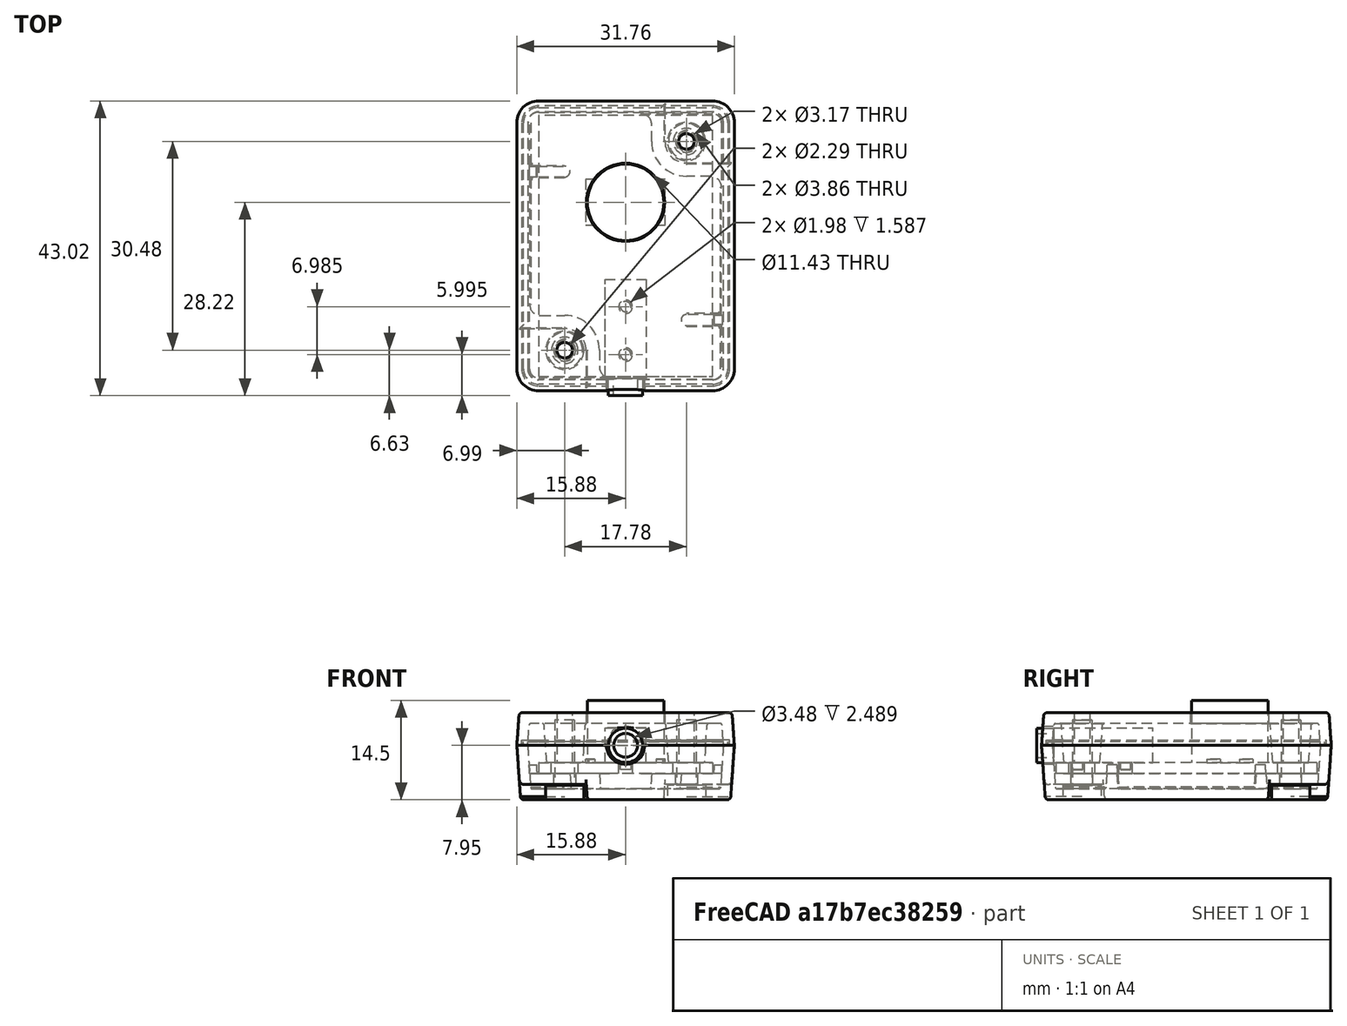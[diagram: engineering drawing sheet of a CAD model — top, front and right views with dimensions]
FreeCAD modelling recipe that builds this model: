
FCSTD DOCUMENT  (FreeCAD 0.20R29603 (Git))
Label: pump-fob-case-v2
License: All rights reserved
LicenseURL: http://en.wikipedia.org/wiki/All_rights_reserved
objects: Sketcher::SketchObject×21, PartDesign::Body×13, PartDesign::Pad×11, PartDesign::Pocket×10, PartDesign::FeatureBase×8, App::DocumentObjectGroup×5, PartDesign::Fillet×5, Mesh::Feature×2, Part::MultiFuse×1, Part::Feature×1
note: 96 computed .brp shape members not serialized (recipe doc carries the construction recipe); baked Part::Feature solids carry a one-line shape summary decoded from their .brp

FEATURE [Sketcher::SketchObject] Sketch  label="audio jack plan"
  FullyConstrained = true
  MapMode = 5
  Support = -> [XY_Plane]
  sketch-geometry (6):
    g0: LineSegment StartX=-2.9972 StartY=14.478 StartZ=0 EndX=2.9972 EndY=14.478 EndZ=0
    g1: LineSegment StartX=2.9972 StartY=14.478 StartZ=0 EndX=2.9972 EndY=0 EndZ=0
    g2: LineSegment StartX=2.9972 StartY=0 StartZ=0 EndX=-2.9972 EndY=0 EndZ=0
    g3: LineSegment StartX=-2.9972 StartY=0 StartZ=0 EndX=-2.9972 EndY=14.478 EndZ=0
    g4: LineSegment StartX=-2.9972 StartY=14.478 StartZ=0 EndX=0 EndY=7.239 EndZ=0
    g5: LineSegment StartX=0 StartY=7.239 StartZ=0 EndX=2.9972 EndY=0 EndZ=0
  constraints (17):
    c: Coincident(g0,g1)
    c: Coincident(g1,g2)
    c: Coincident(g2,g3)
    c: Coincident(g3,g0)
    c: Horizontal(g0)
    c: Horizontal(g2)
    c: Vertical(g1)
    c: Vertical(g3)
    c: PointOnObject(g-1,g2)
    c: Coincident(g0,g4)
    c: Coincident(g4,g5)
    c: Coincident(g5,g1)
    c: Parallel(g4,g5)
    c: Equal(g4,g5)
    c: PointOnObject(g4,g-2)
    c: DistanceY(g1,g1) = 14.478
    c: DistanceX(g2,g2) = 5.9944
FEATURE [PartDesign::Pad] Pad  label="audio jack slab"
  Direction = (0,0,1)
  Length = 5.08
  Length2 = 10
  Profile = -> Sketch
  ReferenceAxis = -> Sketch [N_Axis]
  Type = 0
FEATURE [Sketcher::SketchObject] Sketch001  label="audio jack port plan"
  ExternalGeometry = -> [Pad]
  FullyConstrained = true
  MapMode = 5
  Placement = pos=(0,0,0) rot=(1,0,0;1.5708rad)
  Support = -> [Pad]
  sketch-geometry (4):
    g0: LineSegment StartX=-2.9972 StartY=5.08 StartZ=0 EndX=0 EndY=2.54 EndZ=0
    g1: LineSegment StartX=0 StartY=2.54 StartZ=0 EndX=2.9972 EndY=0 EndZ=0
    g2: Circle CenterX=0 CenterY=2.54 CenterZ=0 NormalX=0 NormalY=0 NormalZ=1 AngleXU=0 Radius=2.5019
    g3: Circle CenterX=0 CenterY=2.54 CenterZ=0 NormalX=0 NormalY=0 NormalZ=1 AngleXU=0 Radius=1.7399
  constraints (9):
    c: Coincident(g0,g-3)
    c: Coincident(g0,g1)
    c: Coincident(g1,g-4)
    c: Parallel(g1,g0)
    c: Equal(g0,g1)
    c: Coincident(g2,g0)
    c: Coincident(g3,g2)
    c: Diameter(g2) = 5.0038
    c: Diameter(g3) = 3.4798
FEATURE [PartDesign::Pad] Pad001  label="audio jack with port"
  BaseFeature = -> Pad
  Direction = (0,-1,2e-16)
  Length = 2.4892
  Length2 = 10
  Profile = -> Sketch001
  ReferenceAxis = -> Sketch001 [N_Axis]
  Type = 0
FEATURE [Sketcher::SketchObject] Sketch002  label="audio jack post plan"
  FullyConstrained = true
  MapMode = 5
  Placement = pos=(0,0,0) rot=(1,0,0;3.14159rad)
  Support = -> [Pad001]
  sketch-geometry (2):
    g0: Circle CenterX=0 CenterY=-3.5052 CenterZ=0 NormalX=0 NormalY=0 NormalZ=1 AngleXU=0 Radius=0.7493
    g1: Circle CenterX=0 CenterY=-10.5156 CenterZ=0 NormalX=0 NormalY=0 NormalZ=1 AngleXU=0 Radius=0.7493
  constraints (6):
    c: PointOnObject(g0,g-2)
    c: PointOnObject(g1,g-2)
    c: Equal(g1,g0)
    c: Diameter(g1) = 1.4986
    c: DistanceY(g0,g-1) = 3.5052
    c: DistanceY(g1,g0) = 7.0104
FEATURE [PartDesign::Pad] Pad002  label="audio jack with posts"
  BaseFeature = -> Pad001
  Direction = (0,0,-1)
  Length = 1.016
  Length2 = 10
  Profile = -> Sketch002
  ReferenceAxis = -> Sketch002 [N_Axis]
  Type = 0
FEATURE [PartDesign::Body] Body  label="audio jack body"
  Group = -> [Sketch,Pad,Sketch001,Pad001,Sketch002,Pad002]
  Origin = -> Origin
  Tip = -> Pad002
FEATURE [Sketcher::SketchObject] Sketch003  label="switch button plan"
  FullyConstrained = true
  MapMode = 5
  Support = -> [XY_Plane001]
  sketch-geometry (1):
    g0: Circle CenterX=0 CenterY=0 CenterZ=0 NormalX=0 NormalY=0 NormalZ=1 AngleXU=0 Radius=5.588
  constraints (2):
    c: Coincident(g0,g-1)
    c: Diameter(g0) = 11.176
FEATURE [PartDesign::Pad] Pad003  label="switch button block"
  Direction = (0,0,1)
  Length = 9.0932
  Length2 = 10
  Profile = -> Sketch003
  ReferenceAxis = -> Sketch003 [N_Axis]
  Type = 0
FEATURE [Sketcher::SketchObject] Sketch004  label="switch lead plan"
  FullyConstrained = true
  MapMode = 5
  Placement = pos=(0,0,0) rot=(1,0,0;3.14159rad)
  Support = -> [Pad003]
  sketch-geometry (22):
    g0: LineSegment StartX=-3.3401 StartY=5.8039 StartZ=0 EndX=-1.397 EndY=5.8039 EndZ=0
    g1: LineSegment StartX=-1.397 StartY=5.8039 StartZ=0 EndX=-1.397 EndY=2.54 EndZ=0
    g2: LineSegment StartX=-1.397 StartY=2.54 StartZ=0 EndX=-3.3401 EndY=2.54 EndZ=0
    g3: LineSegment StartX=-3.3401 StartY=2.54 StartZ=0 EndX=-3.3401 EndY=5.8039 EndZ=0
    g4: LineSegment StartX=1.397 StartY=5.8039 StartZ=0 EndX=3.3401 EndY=5.8039 EndZ=0
    g5: LineSegment StartX=3.3401 StartY=5.8039 StartZ=0 EndX=3.3401 EndY=2.54 EndZ=0
    g6: LineSegment StartX=3.3401 StartY=2.54 StartZ=0 EndX=1.397 EndY=2.54 EndZ=0
    g7: LineSegment StartX=1.397 StartY=2.54 StartZ=0 EndX=1.397 EndY=5.8039 EndZ=0
    g8: LineSegment StartX=1.397 StartY=-2.54 StartZ=0 EndX=3.3401 EndY=-2.54 EndZ=0
    g9: LineSegment StartX=3.3401 StartY=-2.54 StartZ=0 EndX=3.3401 EndY=-5.8039 EndZ=0
    g10: LineSegment StartX=3.3401 StartY=-5.8039 StartZ=0 EndX=1.397 EndY=-5.8039 EndZ=0
    g11: LineSegment StartX=1.397 StartY=-5.8039 StartZ=0 EndX=1.397 EndY=-2.54 EndZ=0
    g12: LineSegment StartX=-3.3401 StartY=-2.54 StartZ=0 EndX=-1.397 EndY=-2.54 EndZ=0
    g13: LineSegment StartX=-1.397 StartY=-2.54 StartZ=0 EndX=-1.397 EndY=-5.8039 EndZ=0
    g14: LineSegment StartX=-1.397 StartY=-5.8039 StartZ=0 EndX=-3.3401 EndY=-5.8039 EndZ=0
    g15: LineSegment StartX=-3.3401 StartY=-5.8039 StartZ=0 EndX=-3.3401 EndY=-2.54 EndZ=0
    g16: LineSegment StartX=-1.397 StartY=2.54 StartZ=0 EndX=1.397 EndY=2.54 EndZ=0
    g17: LineSegment StartX=1.397 StartY=2.54 StartZ=0 EndX=1.397 EndY=-2.54 EndZ=0
    g18: LineSegment StartX=1.397 StartY=-2.54 StartZ=0 EndX=-1.397 EndY=-2.54 EndZ=0
    g19: LineSegment StartX=-1.397 StartY=-2.54 StartZ=0 EndX=-1.397 EndY=2.54 EndZ=0
    g20: LineSegment StartX=-1.397 StartY=2.54 StartZ=0 EndX=0 EndY=0 EndZ=0
    g21: LineSegment StartX=0 StartY=0 StartZ=0 EndX=1.397 EndY=-2.54 EndZ=0
  constraints (60):
    c: Coincident(g0,g1)
    c: Coincident(g1,g2)
    c: Coincident(g2,g3)
    c: Coincident(g3,g0)
    c: Horizontal(g0)
    c: Horizontal(g2)
    c: Vertical(g1)
    c: Vertical(g3)
    c: Coincident(g4,g5)
    c: Coincident(g5,g6)
    c: Coincident(g6,g7)
    c: Coincident(g7,g4)
    c: Horizontal(g4)
    c: Horizontal(g6)
    c: Vertical(g5)
    c: Vertical(g7)
    c: Coincident(g8,g9)
    c: Coincident(g9,g10)
    c: Coincident(g10,g11)
    c: Coincident(g11,g8)
    c: Horizontal(g8)
    c: Horizontal(g10)
    c: Vertical(g9)
    c: Vertical(g11)
    c: Coincident(g12,g13)
    c: Coincident(g13,g14)
    c: Coincident(g14,g15)
    c: Coincident(g15,g12)
    c: Horizontal(g12)
    c: Horizontal(g14)
    c: Vertical(g13)
    c: Vertical(g15)
    c: Coincident(g16,g17)
    c: Coincident(g17,g18)
    c: Coincident(g18,g19)
    c: Coincident(g19,g16)
    c: Horizontal(g16)
    c: Horizontal(g18)
    c: Vertical(g17)
    c: Vertical(g19)
    c: Coincident(g16,g1)
    c: Coincident(g17,g8)
    c: Coincident(g6,g16)
    c: Coincident(g12,g18)
    c: Coincident(g1,g20)
    c: Coincident(g20,g-1)
    c: Coincident(g20,g21)
    c: Coincident(g21,g8)
    c: Parallel(g21,g20)
    c: Equal(g20,g21)
    c: Equal(g6,g8)
    c: Equal(g8,g12)
    c: Equal(g12,g2)
    c: Equal(g7,g1)
    c: Equal(g1,g13)
    c: Equal(g13,g11)
    c: DistanceX(g13,g10) = 2.794
    c: DistanceY(g14,g0) = 11.6078
    c: DistanceX(g0,g4) = 6.6802
    c: DistanceY(g8,g5) = 5.08
FEATURE [PartDesign::Pad] Pad004  label="switch with leads"
  BaseFeature = -> Pad003
  Direction = (0,0,-1)
  Length = 0.508
  Length2 = 10
  Profile = -> Sketch004
  ReferenceAxis = -> Sketch004 [N_Axis]
  Reversed = true
  Type = 0
FEATURE [PartDesign::Body] Body001  label="switch body"
  Group = -> [Sketch003,Pad003,Sketch004,Pad004]
  Origin = -> Origin001
  Tip = -> Pad004
FEATURE [PartDesign::FeatureBase] Clone
  BaseFeature = -> Body
FEATURE [PartDesign::Body] Body002  label="audio jack clone"
  Group = -> [Clone]
  Origin = -> Origin002
  Placement = pos=(0,-0.3302,0) rot=(0,0,1;0rad)
  Tip = -> Clone
FEATURE [PartDesign::FeatureBase] Clone001
  BaseFeature = -> Body001
FEATURE [PartDesign::Body] Body003  label="switch clone"
  Group = -> [Clone001]
  Origin = -> Origin003
  Placement = pos=(0,25.4,0) rot=(0,0,1;1.5708rad)
  Tip = -> Clone001
FEATURE [Sketcher::SketchObject] Sketch005  label="bare pcb plan"
  FullyConstrained = true
  MapMode = 5
  Support = -> [XY_Plane004]
  sketch-geometry (14):
    g0: LineSegment StartX=-12.7 StartY=0 StartZ=0 EndX=12.7 EndY=0 EndZ=0
    g1: LineSegment StartX=12.7 StartY=0 StartZ=0 EndX=12.7 EndY=38.1 EndZ=0
    g2: LineSegment StartX=12.7 StartY=38.1 StartZ=0 EndX=-12.7 EndY=38.1 EndZ=0
    g3: LineSegment StartX=-12.7 StartY=38.1 StartZ=0 EndX=-12.7 EndY=0 EndZ=0
    g4: LineSegment StartX=12.7 StartY=38.1 StartZ=0 EndX=8.89 EndY=38.1 EndZ=0
    g5: LineSegment StartX=8.89 StartY=38.1 StartZ=0 EndX=8.89 EndY=34.29 EndZ=0
    g6: LineSegment StartX=-12.7 StartY=0 StartZ=0 EndX=-8.89 EndY=0 EndZ=0
    g7: LineSegment StartX=-8.89 StartY=0 StartZ=0 EndX=-8.89 EndY=3.81 EndZ=0
    g8: Circle CenterX=-8.89 CenterY=3.81 CenterZ=0 NormalX=0 NormalY=0 NormalZ=1 AngleXU=0 Radius=1.9304
    g9: Circle CenterX=8.89 CenterY=34.29 CenterZ=0 NormalX=0 NormalY=0 NormalZ=1 AngleXU=0 Radius=1.9304
    g10: LineSegment StartX=-12.7 StartY=38.1 StartZ=0 EndX=0 EndY=19.05 EndZ=0
    g11: LineSegment StartX=0 StartY=19.05 StartZ=0 EndX=12.7 EndY=0 EndZ=0
    g12: Circle CenterX=0 CenterY=3.175 CenterZ=0 NormalX=0 NormalY=0 NormalZ=1 AngleXU=0 Radius=0.9906
    g13: Circle CenterX=0 CenterY=10.16 CenterZ=0 NormalX=0 NormalY=0 NormalZ=1 AngleXU=0 Radius=0.9906
  constraints (39):
    c: Coincident(g0,g1)
    c: Coincident(g1,g2)
    c: Coincident(g2,g3)
    c: Coincident(g3,g0)
    c: Horizontal(g0)
    c: Horizontal(g2)
    c: Vertical(g1)
    c: Vertical(g3)
    c: DistanceY(g1,g1) = 38.1
    c: DistanceX(g2,g2) = 25.4
    c: Coincident(g1,g4)
    c: Coincident(g4,g5)
    c: Vertical(g5)
    c: Coincident(g0,g6)
    c: Coincident(g6,g7)
    c: Vertical(g7)
    c: Equal(g5,g7)
    c: Equal(g4,g6)
    c: Horizontal(g6)
    c: Horizontal(g4)
    c: DistanceX(g0,g6) = 3.81
    c: DistanceY(g0,g7) = 3.81
    c: Coincident(g8,g7)
    c: Coincident(g9,g5)
    c: Equal(g9,g8)
    c: Diameter(g9) = 3.8608
    c: PointOnObject(g-1,g0)
    c: Coincident(g2,g10)
    c: PointOnObject(g10,g-2)
    c: Coincident(g10,g11)
    c: Coincident(g11,g0)
    c: Parallel(g11,g10)
    c: Equal(g10,g11)
    c: PointOnObject(g12,g-2)
    c: PointOnObject(g13,g-2)
    c: Equal(g12,g13)
    c: Diameter(g12) = 1.9812
    c: DistanceY(g0,g12) = 3.175
    c: DistanceY(g12,g13) = 6.985
FEATURE [PartDesign::Pad] Pad005  label="bare pcb slab"
  Direction = (0,0,1)
  Length = 1.5875
  Length2 = 10
  Profile = -> Sketch005
  ReferenceAxis = -> Sketch005 [N_Axis]
  Reversed = true
  Type = 0
FEATURE [PartDesign::Body] Body004  label="bare pcb body"
  Group = -> [Sketch005,Pad005]
  Origin = -> Origin004
  Tip = -> Pad005
FEATURE [PartDesign::FeatureBase] Clone002
  BaseFeature = -> Body004
FEATURE [PartDesign::Body] Body005  label="bare pcb clone"
  Group = -> [Clone002]
  Origin = -> Origin005
  Tip = -> Clone002
FEATURE [Part::MultiFuse] Fusion  label="populated pcb"
  Shapes = -> [Body002,Body003,Body005]
FEATURE [App::DocumentObjectGroup] Group  label="pcb parts"
  Group = -> [Body,Body001,Body004,Fusion]
FEATURE [PartDesign::FeatureBase] Clone003
  BaseFeature = -> Fusion
FEATURE [PartDesign::Body] Body006  label="populated pcb clone"
  Group = -> [Clone003]
  Origin = -> Origin006
  Placement = pos=(0,0,-2.54) rot=(0,0,1;0rad)
  Tip = -> Clone003
FEATURE [Sketcher::SketchObject] Sketch006  label="bottom shell outline"
  FullyConstrained = true
  MapMode = 5
  Support = -> [XY_Plane007]
  sketch-geometry (37):
    g0: LineSegment StartX=0 StartY=1.0795 StartZ=0 EndX=12.7 EndY=1.0795 EndZ=0
    g1: LineSegment StartX=12.7 StartY=1.0795 StartZ=0 EndX=14.2875 EndY=1.0795 EndZ=0
    g2: LineSegment StartX=14.2875 StartY=1.0795 StartZ=0 EndX=15.875 EndY=1.0795 EndZ=0
    g3: LineSegment StartX=12.7 StartY=1.0795 StartZ=0 EndX=12.7 EndY=37.0205 EndZ=0
    g4: LineSegment StartX=12.7 StartY=37.0205 StartZ=0 EndX=14.2875 EndY=37.0205 EndZ=0
    g5: LineSegment StartX=14.2875 StartY=37.0205 StartZ=0 EndX=15.875 EndY=37.0205 EndZ=0
    g6: LineSegment StartX=12.7 StartY=40.1955 StartZ=0 EndX=12.7 EndY=38.608 EndZ=0
    g7: LineSegment StartX=12.7 StartY=38.608 StartZ=0 EndX=12.7 EndY=37.0205 EndZ=0
    g8: LineSegment StartX=12.7 StartY=37.0205 StartZ=0 EndX=-12.7 EndY=37.0205 EndZ=0
    g9: LineSegment StartX=-12.7 StartY=37.0205 StartZ=0 EndX=-12.7 EndY=38.608 EndZ=0
    g10: LineSegment StartX=-12.7 StartY=38.608 StartZ=0 EndX=-12.7 EndY=40.1955 EndZ=0
    g11: LineSegment StartX=-15.875 StartY=37.0205 StartZ=0 EndX=-14.2875 EndY=37.0205 EndZ=0
    g12: LineSegment StartX=-14.2875 StartY=37.0205 StartZ=0 EndX=-12.7 EndY=37.0205 EndZ=0
    g13: LineSegment StartX=-12.7 StartY=37.0205 StartZ=0 EndX=-12.7 EndY=1.0795 EndZ=0
    g14: LineSegment StartX=-12.7 StartY=1.0795 StartZ=0 EndX=-14.2875 EndY=1.0795 EndZ=0
    g15: LineSegment StartX=-14.2875 StartY=1.0795 StartZ=0 EndX=-15.875 EndY=1.0795 EndZ=0
    g16: LineSegment StartX=-12.7 StartY=-2.0955 StartZ=0 EndX=-12.7 EndY=-0.508 EndZ=0
    g17: LineSegment StartX=-12.7 StartY=-0.508 StartZ=0 EndX=-12.7 EndY=1.0795 EndZ=0
    g18: LineSegment StartX=-12.7 StartY=1.0795 StartZ=0 EndX=0 EndY=1.0795 EndZ=0
    g19: LineSegment StartX=12.7 StartY=1.0795 StartZ=0 EndX=12.7 EndY=-0.508 EndZ=0
    g20: LineSegment StartX=12.7 StartY=-0.508 StartZ=0 EndX=12.7 EndY=-2.0955 EndZ=0
    g21: LineSegment StartX=-14.2875 StartY=37.0205 StartZ=0 EndX=-14.2875 EndY=1.0795 EndZ=0
    g22: LineSegment StartX=-15.875 StartY=1.0795 StartZ=0 EndX=-15.875 EndY=37.0205 EndZ=0
    g23: LineSegment StartX=14.2875 StartY=1.0795 StartZ=0 EndX=14.2875 EndY=37.0205 EndZ=0
    g24: LineSegment StartX=15.875 StartY=1.0795 StartZ=0 EndX=15.875 EndY=37.0205 EndZ=0
    g25: LineSegment StartX=12.7 StartY=38.608 StartZ=0 EndX=-12.7 EndY=38.608 EndZ=0
    g26: LineSegment StartX=-12.7 StartY=40.1955 StartZ=0 EndX=12.7 EndY=40.1955 EndZ=0
    g27: LineSegment StartX=-12.7 StartY=-0.508 StartZ=0 EndX=12.7 EndY=-0.508 EndZ=0
    g28: LineSegment StartX=12.7 StartY=-2.0955 StartZ=0 EndX=-12.7 EndY=-2.0955 EndZ=0
    g29: ArcOfCircle CenterX=12.7 CenterY=1.0795 CenterZ=0 NormalX=0 NormalY=0 NormalZ=1 AngleXU=0 Radius=1.5875 StartAngle=4.71239 EndAngle=6.28319
    g30: ArcOfCircle CenterX=12.7 CenterY=1.0795 CenterZ=0 NormalX=0 NormalY=0 NormalZ=1 AngleXU=0 Radius=3.175 StartAngle=4.71239 EndAngle=6.28319
    g31: ArcOfCircle CenterX=12.7 CenterY=37.0205 CenterZ=0 NormalX=0 NormalY=0 NormalZ=1 AngleXU=0 Radius=1.5875 StartAngle=0 EndAngle=1.5708
    g32: ArcOfCircle CenterX=12.7 CenterY=37.0205 CenterZ=0 NormalX=0 NormalY=0 NormalZ=1 AngleXU=0 Radius=3.175 StartAngle=0 EndAngle=1.5708
    g33: ArcOfCircle CenterX=-12.7 CenterY=37.0205 CenterZ=0 NormalX=0 NormalY=0 NormalZ=1 AngleXU=0 Radius=1.5875 StartAngle=1.5708 EndAngle=3.14159
    g34: ArcOfCircle CenterX=-12.7 CenterY=37.0205 CenterZ=0 NormalX=0 NormalY=0 NormalZ=1 AngleXU=0 Radius=3.175 StartAngle=1.5708 EndAngle=3.14159
    g35: ArcOfCircle CenterX=-12.7 CenterY=1.0795 CenterZ=0 NormalX=0 NormalY=0 NormalZ=1 AngleXU=0 Radius=1.5875 StartAngle=3.14159 EndAngle=4.71239
    g36: ArcOfCircle CenterX=-12.7 CenterY=1.0795 CenterZ=0 NormalX=0 NormalY=0 NormalZ=1 AngleXU=0 Radius=3.175 StartAngle=3.14159 EndAngle=4.71239
  constraints (95):
    c: Coincident(g0,g1)
    c: Horizontal(g1)
    c: Coincident(g1,g2)
    c: Horizontal(g2)
    c: Coincident(g0,g3)
    c: Vertical(g3)
    c: Coincident(g3,g4)
    c: Horizontal(g4)
    c: Coincident(g4,g5)
    c: Horizontal(g5)
    c: Vertical(g6)
    c: Coincident(g6,g7)
    c: Coincident(g7,g3)
    c: Vertical(g7)
    c: Coincident(g7,g8)
    c: Horizontal(g8)
    c: Coincident(g8,g9)
    c: Vertical(g9)
    c: Coincident(g9,g10)
    c: Vertical(g10)
    c: Horizontal(g11)
    c: Coincident(g11,g12)
    c: Coincident(g12,g8)
    c: Horizontal(g12)
    c: Coincident(g12,g13)
    c: Vertical(g13)
    c: Coincident(g13,g14)
    c: Horizontal(g14)
    c: Coincident(g14,g15)
    c: Horizontal(g15)
    c: Vertical(g16)
    c: Coincident(g16,g17)
    c: Coincident(g17,g13)
    c: Vertical(g17)
    c: Coincident(g17,g18)
    c: Coincident(g18,g0)
    c: Coincident(g0,g19)
    c: Vertical(g19)
    c: Coincident(g19,g20)
    c: Vertical(g20)
    c: Horizontal(g18)
    c: Horizontal(g0)
    c: Coincident(g21,g11)
    c: Vertical(g21)
    c: Coincident(g22,g15)
    c: Coincident(g22,g11)
    c: Vertical(g22)
    c: Coincident(g23,g1)
    c: Coincident(g23,g4)
    c: Vertical(g23)
    c: Coincident(g24,g2)
    c: Coincident(g24,g5)
    c: Vertical(g24)
    c: Coincident(g25,g6)
    c: Coincident(g25,g9)
    c: Horizontal(g25)
    c: Coincident(g26,g10)
    c: Coincident(g26,g6)
    c: Coincident(g27,g16)
    c: Coincident(g27,g19)
    c: Coincident(g28,g20)
    c: Coincident(g28,g16)
    c: Coincident(g14,g21)
    c: Horizontal(g26)
    c: Coincident(g29,g0)
    c: Coincident(g29,g27)
    c: Coincident(g29,g23)
    c: Coincident(g30,g29)
    c: Coincident(g30,g28)
    c: Coincident(g30,g24)
    c: Coincident(g31,g3)
    c: Coincident(g31,g23)
    c: Coincident(g31,g25)
    c: Coincident(g32,g31)
    c: Coincident(g32,g24)
    c: Coincident(g32,g26)
    c: Coincident(g33,g8)
    c: Coincident(g33,g25)
    c: Coincident(g33,g21)
    c: Coincident(g34,g33)
    c: Coincident(g34,g26)
    c: Coincident(g34,g22)
    c: Coincident(g35,g13)
    c: Coincident(g35,g21)
    c: Coincident(g35,g27)
    c: Coincident(g36,g35)
    c: Coincident(g36,g22)
    c: Coincident(g36,g28)
    c: Equal(g18,g0)
    c: DistanceX(g35,g29) = 25.4
    c: DistanceX(g22,g35) = 3.175
    c: DistanceX(g15,g15) = 1.5875
    c: DistanceY(g27,g25) = 39.116
    c: PointOnObject(g0,g-2)
    c: DistanceY(g19,g-1) = 0.508
FEATURE [PartDesign::Pad] Pad006  label="bottom shell block"
  Direction = (0,0,1)
  Length = 7.9375
  Length2 = 10
  Profile = -> Sketch006
  ReferenceAxis = -> Sketch006 [N_Axis]
  Reversed = true
  TaperAngle = -4
  Type = 0
FEATURE [Sketcher::SketchObject] Sketch007  label="bottom shell first hollow plan"
  ExternalGeometry = -> [Pad006]
  FullyConstrained = true
  MapMode = 5
  Support = -> [Pad006]
  sketch-geometry (21):
    g0: LineSegment StartX=-14.2875 StartY=37.0205 StartZ=0 EndX=-12.7 EndY=37.0205 EndZ=0
    g1: LineSegment StartX=-12.7 StartY=37.0205 StartZ=0 EndX=-12.7 EndY=38.608 EndZ=0
    g2: LineSegment StartX=-12.7 StartY=38.608 StartZ=0 EndX=12.7 EndY=38.608 EndZ=0
    g3: LineSegment StartX=12.7 StartY=38.608 StartZ=0 EndX=12.7 EndY=37.0205 EndZ=0
    g4: LineSegment StartX=12.7 StartY=37.0205 StartZ=0 EndX=14.2875 EndY=37.0205 EndZ=0
    g5: LineSegment StartX=14.2875 StartY=37.0205 StartZ=0 EndX=14.2875 EndY=1.0795 EndZ=0
    g6: LineSegment StartX=14.2875 StartY=1.0795 StartZ=0 EndX=12.7 EndY=1.0795 EndZ=0
    g7: LineSegment StartX=12.7 StartY=1.0795 StartZ=0 EndX=12.7 EndY=-0.508 EndZ=0
    g8: LineSegment StartX=12.7 StartY=-0.508 StartZ=0 EndX=-12.7 EndY=-0.508 EndZ=0
    g9: LineSegment StartX=-12.7 StartY=-0.508 StartZ=0 EndX=-12.7 EndY=1.0795 EndZ=0
    g10: LineSegment StartX=-12.7 StartY=1.0795 StartZ=0 EndX=-14.2875 EndY=1.0795 EndZ=0
    g11: LineSegment StartX=-14.2875 StartY=1.0795 StartZ=0 EndX=-14.2875 EndY=37.0205 EndZ=0
    g12: ArcOfCircle CenterX=-12.7 CenterY=37.0205 CenterZ=0 NormalX=0 NormalY=0 NormalZ=1 AngleXU=0 Radius=1.5875 StartAngle=1.5708 EndAngle=3.14159
    g13: ArcOfCircle CenterX=-12.7 CenterY=1.0795 CenterZ=0 NormalX=0 NormalY=0 NormalZ=1 AngleXU=0 Radius=1.5875 StartAngle=3.14159 EndAngle=4.71239
    g14: ArcOfCircle CenterX=12.7 CenterY=1.0795 CenterZ=0 NormalX=0 NormalY=0 NormalZ=1 AngleXU=0 Radius=1.5875 StartAngle=4.71239 EndAngle=6.28319
    g15: ArcOfCircle CenterX=12.7 CenterY=37.0205 CenterZ=0 NormalX=0 NormalY=0 NormalZ=1 AngleXU=0 Radius=1.5875 StartAngle=5e-16 EndAngle=1.5708
    g16: LineSegment StartX=0 StartY=0 StartZ=0 EndX=12.7 EndY=0 EndZ=0
    g17: LineSegment StartX=12.7 StartY=0 StartZ=0 EndX=12.7 EndY=38.1 EndZ=0
    g18: LineSegment StartX=12.7 StartY=38.1 StartZ=0 EndX=-12.7 EndY=38.1 EndZ=0
    g19: LineSegment StartX=-12.7 StartY=38.1 StartZ=0 EndX=-12.7 EndY=0 EndZ=0
    g20: LineSegment StartX=-12.7 StartY=0 StartZ=0 EndX=0 EndY=0 EndZ=0
  constraints (54):
    c: Coincident(g0,g-3)
    c: Horizontal(g0)
    c: Coincident(g0,g1)
    c: Vertical(g1)
    c: Coincident(g1,g2)
    c: Horizontal(g2)
    c: Coincident(g2,g3)
    c: Coincident(g3,g-4)
    c: Vertical(g3)
    c: Coincident(g3,g4)
    c: Horizontal(g4)
    c: Coincident(g4,g5)
    c: Vertical(g5)
    c: Coincident(g5,g6)
    c: Coincident(g6,g-5)
    c: Horizontal(g6)
    c: Coincident(g6,g7)
    c: Vertical(g7)
    c: Coincident(g7,g8)
    c: Coincident(g8,g9)
    c: Coincident(g9,g-6)
    c: Vertical(g9)
    c: Coincident(g9,g10)
    c: Horizontal(g10)
    c: Coincident(g10,g11)
    c: Coincident(g11,g0)
    c: Vertical(g11)
    c: Coincident(g12,g0)
    c: Coincident(g12,g2)
    c: Coincident(g12,g11)
    c: Coincident(g13,g9)
    c: Coincident(g13,g11)
    c: Coincident(g13,g8)
    c: Coincident(g14,g6)
    c: Coincident(g14,g8)
    c: Coincident(g14,g5)
    c: Coincident(g15,g3)
    c: Coincident(g15,g2)
    c: Coincident(g15,g5)
    c: DistanceX(g-6,g11) = 1.5875
    c: Coincident(g-1,g16)
    c: Coincident(g16,g17)
    c: Vertical(g17)
    c: Coincident(g17,g18)
    c: Horizontal(g18)
    c: Coincident(g18,g19)
    c: Vertical(g19)
    c: Coincident(g19,g20)
    c: Coincident(g20,g16)
    c: Equal(g20,g16)
    c: Horizontal(g20)
    c: Horizontal(g16)
    c: DistanceX(g18,g18) = 25.4
    c: DistanceY(g17,g17) = 38.1
FEATURE [PartDesign::Pocket] Pocket  label="bottom shell with first hollow"
  BaseFeature = -> Pad006
  Direction = (0,0,-1)
  Length = 4.1402
  Length2 = 5
  Profile = -> Sketch007
  ReferenceAxis = -> Sketch007 [N_Axis]
  TaperAngle = -4
  Type = 0
FEATURE [Sketcher::SketchObject] Sketch008  label="bottom shell second hollow plan"
  ExternalGeometry = -> [Pocket]
  FullyConstrained = true
  MapMode = 5
  Placement = pos=(0,0,-4.1402) rot=(0,0,1;0rad)
  Support = -> [Pocket]
  sketch-geometry (50):
    g0: LineSegment StartX=-12.7 StartY=0 StartZ=0 EndX=-8.89 EndY=0 EndZ=0
    g1: LineSegment StartX=-8.89 StartY=0 StartZ=0 EndX=-8.89 EndY=3.81 EndZ=0
    g2: LineSegment StartX=12.7 StartY=38.1 StartZ=0 EndX=8.89 EndY=38.1 EndZ=0
    g3: LineSegment StartX=8.89 StartY=38.1 StartZ=0 EndX=8.89 EndY=34.29 EndZ=0
    g4: LineSegment StartX=-12.7 StartY=38.3185 StartZ=0 EndX=-12.7 EndY=37.0205 EndZ=0
    g5: LineSegment StartX=-12.7 StartY=37.0205 StartZ=0 EndX=-13.998 EndY=37.0205 EndZ=0
    g6: LineSegment StartX=-13.998 StartY=37.0205 StartZ=0 EndX=-13.998 EndY=30.6705 EndZ=0
    g7: LineSegment StartX=-13.998 StartY=30.6705 StartZ=0 EndX=-13.998 EndY=29.0703 EndZ=0
    g8: LineSegment StartX=-13.998 StartY=29.0703 StartZ=0 EndX=-13.998 EndY=10.4775 EndZ=0
    g9: LineSegment StartX=-13.998 StartY=10.4775 StartZ=0 EndX=-12.4105 EndY=10.4775 EndZ=0
    g10: LineSegment StartX=-12.4105 StartY=10.4775 StartZ=0 EndX=-12.4105 EndY=8.89 EndZ=0
    g11: LineSegment StartX=-12.4105 StartY=8.89 StartZ=0 EndX=-8.89 EndY=8.89 EndZ=0
    g12: LineSegment StartX=-8.89 StartY=8.89 StartZ=0 EndX=-8.89 EndY=3.81 EndZ=0
    g13: LineSegment StartX=-8.89 StartY=3.81 StartZ=0 EndX=-3.81 EndY=3.81 EndZ=0
    g14: LineSegment StartX=-3.81 StartY=3.81 StartZ=0 EndX=-3.81 EndY=1.36901 EndZ=0
    g15: LineSegment StartX=-3.81 StartY=1.36901 StartZ=0 EndX=-2.2225 EndY=1.36901 EndZ=0
    g16: LineSegment StartX=-2.2225 StartY=1.36901 StartZ=0 EndX=-2.2225 EndY=-0.218489 EndZ=0
    g17: LineSegment StartX=-2.2225 StartY=-0.218489 StartZ=0 EndX=12.7 EndY=-0.218489 EndZ=0
    g18: LineSegment StartX=12.7 StartY=-0.218489 StartZ=0 EndX=12.7 EndY=1.0795 EndZ=0
    g19: LineSegment StartX=12.7 StartY=1.0795 StartZ=0 EndX=13.998 EndY=1.0795 EndZ=0
    g20: LineSegment StartX=13.998 StartY=1.0795 StartZ=0 EndX=13.998 EndY=7.4295 EndZ=0
    g21: LineSegment StartX=13.998 StartY=7.4295 StartZ=0 EndX=13.998 EndY=9.0297 EndZ=0
    g22: LineSegment StartX=13.998 StartY=9.0297 StartZ=0 EndX=13.998 EndY=27.6225 EndZ=0
    g23: LineSegment StartX=13.998 StartY=27.6225 StartZ=0 EndX=12.4105 EndY=27.6225 EndZ=0
    g24: LineSegment StartX=12.4105 StartY=27.6225 StartZ=0 EndX=12.4105 EndY=29.21 EndZ=0
    g25: LineSegment StartX=12.4105 StartY=29.21 StartZ=0 EndX=8.89 EndY=29.21 EndZ=0
    g26: LineSegment StartX=8.89 StartY=29.21 StartZ=0 EndX=8.89 EndY=34.29 EndZ=0
    g27: LineSegment StartX=8.89 StartY=34.29 StartZ=0 EndX=3.81 EndY=34.29 EndZ=0
    g28: LineSegment StartX=3.81 StartY=34.29 StartZ=0 EndX=3.81 EndY=36.731 EndZ=0
    g29: LineSegment StartX=3.81 StartY=36.731 StartZ=0 EndX=2.2225 EndY=36.731 EndZ=0
    g30: LineSegment StartX=2.2225 StartY=36.731 StartZ=0 EndX=2.2225 EndY=38.3185 EndZ=0
    g31: LineSegment StartX=2.2225 StartY=38.3185 StartZ=0 EndX=-12.7 EndY=38.3185 EndZ=0
    g32: ArcOfCircle CenterX=2.2225 CenterY=36.731 CenterZ=0 NormalX=0 NormalY=0 NormalZ=1 AngleXU=0 Radius=1.5875 StartAngle=0 EndAngle=1.5708
    g33: ArcOfCircle CenterX=8.89 CenterY=34.29 CenterZ=0 NormalX=0 NormalY=0 NormalZ=1 AngleXU=0 Radius=5.08 StartAngle=3.14159 EndAngle=4.71239
    g34: ArcOfCircle CenterX=-12.7 CenterY=37.0205 CenterZ=0 NormalX=0 NormalY=0 NormalZ=1 AngleXU=0 Radius=1.29799 StartAngle=1.5708 EndAngle=3.14159
    g35: ArcOfCircle CenterX=-12.4105 CenterY=10.4775 CenterZ=0 NormalX=0 NormalY=0 NormalZ=1 AngleXU=0 Radius=1.5875 StartAngle=3.14159 EndAngle=4.71239
    g36: ArcOfCircle CenterX=-8.89 CenterY=3.81 CenterZ=0 NormalX=0 NormalY=0 NormalZ=1 AngleXU=0 Radius=5.08 StartAngle=0 EndAngle=1.5708
    g37: ArcOfCircle CenterX=-2.2225 CenterY=1.36901 CenterZ=0 NormalX=0 NormalY=0 NormalZ=1 AngleXU=0 Radius=1.5875 StartAngle=3.14159 EndAngle=4.71239
    g38: ArcOfCircle CenterX=12.7 CenterY=1.0795 CenterZ=0 NormalX=0 NormalY=0 NormalZ=1 AngleXU=0 Radius=1.29799 StartAngle=4.71239 EndAngle=6.28319
    g39: ArcOfCircle CenterX=12.4105 CenterY=27.6225 CenterZ=0 NormalX=0 NormalY=0 NormalZ=1 AngleXU=0 Radius=1.5875 StartAngle=0 EndAngle=1.5708
    g40: LineSegment StartX=-13.998 StartY=30.6705 StartZ=0 EndX=-8.91799 EndY=30.6705 EndZ=0
    g41: LineSegment StartX=-8.91799 StartY=30.6705 StartZ=0 EndX=-8.91799 EndY=29.0703 EndZ=0
    g42: LineSegment StartX=-8.91799 StartY=29.0703 StartZ=0 EndX=-13.998 EndY=29.0703 EndZ=0
    g43: LineSegment StartX=13.998 StartY=9.0297 StartZ=0 EndX=8.91799 EndY=9.0297 EndZ=0
    g44: LineSegment StartX=8.91799 StartY=9.0297 StartZ=0 EndX=8.91799 EndY=7.4295 EndZ=0
    g45: LineSegment StartX=8.91799 StartY=7.4295 StartZ=0 EndX=13.998 EndY=7.4295 EndZ=0
    g46: ArcOfCircle CenterX=-8.91799 CenterY=29.8704 CenterZ=0 NormalX=0 NormalY=0 NormalZ=1 AngleXU=0 Radius=0.8001 StartAngle=4.71239 EndAngle=7.85398
    g47: ArcOfCircle CenterX=8.91799 CenterY=8.2296 CenterZ=0 NormalX=0 NormalY=0 NormalZ=1 AngleXU=0 Radius=0.8001 StartAngle=1.5708 EndAngle=4.71239
    g48: LineSegment StartX=-12.7 StartY=1.0795 StartZ=0 EndX=-12.7 EndY=-0.218489 EndZ=0
    g49: LineSegment StartX=12.7 StartY=37.0205 StartZ=0 EndX=12.7 EndY=38.3185 EndZ=0
  constraints (137):
    c: Horizontal(g0)
    c: Coincident(g0,g1)
    c: Vertical(g1)
    c: Coincident(g2,g-4)
    c: Horizontal(g2)
    c: Coincident(g2,g3)
    c: Vertical(g3)
    c: Equal(g2,g3)
    c: Equal(g3,g1)
    c: Equal(g1,g0)
    c: DistanceY(g3,g2) = 3.81
    c: Coincident(g4,g-3)
    c: Vertical(g4)
    c: Coincident(g4,g5)
    c: Horizontal(g5)
    c: Coincident(g5,g6)
    c: Vertical(g6)
    c: Coincident(g6,g7)
    c: Vertical(g7)
    c: Coincident(g7,g8)
    c: Vertical(g8)
    c: Coincident(g8,g9)
    c: Horizontal(g9)
    c: Coincident(g9,g10)
    c: Vertical(g10)
    c: Coincident(g10,g11)
    c: Horizontal(g11)
    c: Coincident(g11,g12)
    c: Coincident(g12,g1)
    c: Vertical(g12)
    c: Coincident(g12,g13)
    c: Horizontal(g13)
    c: Coincident(g13,g14)
    c: Vertical(g14)
    c: Coincident(g14,g15)
    c: Horizontal(g15)
    c: Coincident(g15,g16)
    c: Vertical(g16)
    c: Coincident(g16,g17)
    c: Horizontal(g17)
    c: Coincident(g17,g18)
    c: Coincident(g18,g-6)
    c: Vertical(g18)
    c: Coincident(g18,g19)
    c: Horizontal(g19)
    c: Coincident(g19,g20)
    c: Vertical(g20)
    c: Coincident(g20,g21)
    c: Vertical(g21)
    c: Coincident(g21,g22)
    c: Vertical(g22)
    c: Coincident(g22,g23)
    c: Horizontal(g23)
    c: Coincident(g23,g24)
    c: Vertical(g24)
    c: Coincident(g24,g25)
    c: Horizontal(g25)
    c: Coincident(g25,g26)
    c: Coincident(g26,g3)
    c: Vertical(g26)
    c: Coincident(g26,g27)
    c: Horizontal(g27)
    c: Coincident(g27,g28)
    c: Vertical(g28)
    c: Coincident(g28,g29)
    c: Horizontal(g29)
    c: Coincident(g29,g30)
    c: Vertical(g30)
    c: Coincident(g30,g31)
    c: Horizontal(g31)
    c: Coincident(g4,g31)
    c: Coincident(g32,g29)
    c: Coincident(g32,g31)
    c: Coincident(g32,g28)
    c: Coincident(g33,g3)
    c: Coincident(g33,g28)
    c: Coincident(g33,g25)
    c: Coincident(g34,g4)
    c: Coincident(g34,g31)
    c: Coincident(g34,g6)
    c: Coincident(g35,g9)
    c: Coincident(g35,g11)
    c: Coincident(g35,g8)
    c: Coincident(g36,g1)
    c: Coincident(g36,g11)
    c: Coincident(g36,g14)
    c: Coincident(g37,g15)
    c: Coincident(g37,g14)
    c: Coincident(g37,g17)
    c: Coincident(g38,g18)
    c: Coincident(g38,g17)
    c: Coincident(g38,g20)
    c: Coincident(g39,g23)
    c: Coincident(g39,g25)
    c: Coincident(g39,g22)
    c: Equal(g39,g32)
    c: Equal(g39,g35)
    c: Equal(g39,g37)
    c: Radius(g39) = 1.5875
    c: Coincident(g6,g40)
    c: Horizontal(g40)
    c: Coincident(g40,g41)
    c: Vertical(g41)
    c: Coincident(g41,g42)
    c: Coincident(g42,g8)
    c: Horizontal(g42)
    c: Coincident(g22,g43)
    c: Horizontal(g43)
    c: Coincident(g43,g44)
    c: Vertical(g44)
    c: Coincident(g44,g45)
    c: Coincident(g45,g20)
    c: Horizontal(g45)
    c: Equal(g41,g44)
    c: Equal(g6,g20)
    c: Equal(g38,g-6)
    c: Equal(g-6,g34)
    c: Equal(g33,g36)
    c: Radius(g36) = 5.08
    c: DistanceY(g7,g7) = 1.6002
    c: DistanceY(g6,g6) = 6.35
    c: Equal(g43,g42)
    c: DistanceX(g45,g45) = 5.08
    c: PointOnObject(g46,g41)
    c: Coincident(g46,g40)
    c: Coincident(g46,g42)
    c: PointOnObject(g47,g44)
    c: Coincident(g47,g43)
    c: Coincident(g47,g45)
    c: Coincident(g48,g-5)
    c: Coincident(g48,g-5)
    c: PointOnObject(g0,g48)
    c: PointOnObject(g0,g-1)
    c: DistanceY(g0,g2) = 38.1
    c: Coincident(g49,g-4)
    c: Coincident(g49,g-4)
    c: PointOnObject(g2,g49)
FEATURE [PartDesign::Pocket] Pocket001  label="bottom shell with second hollow"
  BaseFeature = -> Pocket
  Direction = (0,0,-1)
  Length = 2.2098
  Length2 = 5
  Profile = -> Sketch008
  ReferenceAxis = -> Sketch008 [N_Axis]
  TaperAngle = -4
  Type = 0
FEATURE [Sketcher::SketchObject] Sketch009  label="bottom shell screw hole plan"
  ExternalGeometry = -> [Pocket001]
  FullyConstrained = true
  MapMode = 5
  Placement = pos=(0,0,-4.1402) rot=(0,0,1;0rad)
  Support = -> [Pocket001]
  sketch-geometry (2):
    g0: Circle CenterX=-8.89 CenterY=3.81 CenterZ=0 NormalX=0 NormalY=0 NormalZ=1 AngleXU=0 Radius=1.5875
    g1: Circle CenterX=8.89 CenterY=34.29 CenterZ=0 NormalX=0 NormalY=0 NormalZ=1 AngleXU=0 Radius=1.5875
  constraints (4):
    c: Coincident(g0,g-3)
    c: Coincident(g1,g-4)
    c: Equal(g1,g0)
    c: Diameter(g1) = 3.175
FEATURE [PartDesign::Pocket] Pocket002  label="bottom shell with screw holes"
  BaseFeature = -> Pocket001
  Direction = (0,0,-1)
  Length = 5
  Length2 = 5
  Profile = -> Sketch009
  ReferenceAxis = -> Sketch009 [N_Axis]
  Type = 1
FEATURE [Sketcher::SketchObject] Sketch010  label="bottom shell screw inset plan"
  ExternalGeometry = -> [Pocket002]
  FullyConstrained = true
  MapMode = 5
  Placement = pos=(0,0,-7.9375) rot=(1,0,0;3.14159rad)
  Support = -> [Pocket002]
  sketch-geometry (14):
    g0: LineSegment StartX=-8.89 StartY=-3.81 StartZ=0 EndX=-5.588 EndY=-3.81 EndZ=0
    g1: LineSegment StartX=-5.588 StartY=-3.81 StartZ=0 EndX=-5.588 EndY=5.588 EndZ=0
    g2: LineSegment StartX=-5.588 StartY=5.588 StartZ=0 EndX=-18.288 EndY=5.588 EndZ=0
    g3: LineSegment StartX=-18.288 StartY=5.588 StartZ=0 EndX=-18.288 EndY=-7.112 EndZ=0
    g4: LineSegment StartX=-18.288 StartY=-7.112 StartZ=0 EndX=-8.89 EndY=-7.112 EndZ=0
    g5: LineSegment StartX=-8.89 StartY=-7.112 StartZ=0 EndX=-8.89 EndY=-3.81 EndZ=0
    g6: LineSegment StartX=8.89 StartY=-34.29 StartZ=0 EndX=8.89 EndY=-30.988 EndZ=0
    g7: LineSegment StartX=8.89 StartY=-30.988 StartZ=0 EndX=18.288 EndY=-30.988 EndZ=0
    g8: LineSegment StartX=18.288 StartY=-30.988 StartZ=0 EndX=18.288 EndY=-43.688 EndZ=0
    g9: LineSegment StartX=18.288 StartY=-43.688 StartZ=0 EndX=5.588 EndY=-43.688 EndZ=0
    g10: LineSegment StartX=5.588 StartY=-43.688 StartZ=0 EndX=5.588 EndY=-34.29 EndZ=0
    g11: LineSegment StartX=5.588 StartY=-34.29 StartZ=0 EndX=8.89 EndY=-34.29 EndZ=0
    g12: ArcOfCircle CenterX=-8.89 CenterY=-3.81 CenterZ=0 NormalX=0 NormalY=0 NormalZ=1 AngleXU=0 Radius=3.302 StartAngle=4.71239 EndAngle=6.28319
    g13: ArcOfCircle CenterX=8.89 CenterY=-34.29 CenterZ=0 NormalX=0 NormalY=0 NormalZ=1 AngleXU=0 Radius=3.302 StartAngle=1.5708 EndAngle=3.14159
  constraints (38):
    c: Coincident(g0,g-3)
    c: Horizontal(g0)
    c: Coincident(g0,g1)
    c: Vertical(g1)
    c: Coincident(g1,g2)
    c: Horizontal(g2)
    c: Coincident(g2,g3)
    c: Vertical(g3)
    c: Coincident(g3,g4)
    c: Horizontal(g4)
    c: Coincident(g4,g5)
    c: Coincident(g5,g0)
    c: Vertical(g5)
    c: Coincident(g6,g-4)
    c: Vertical(g6)
    c: Coincident(g6,g7)
    c: Horizontal(g7)
    c: Coincident(g7,g8)
    c: Vertical(g8)
    c: Coincident(g8,g9)
    c: Horizontal(g9)
    c: Coincident(g9,g10)
    c: Vertical(g10)
    c: Coincident(g10,g11)
    c: Coincident(g11,g6)
    c: Horizontal(g11)
    c: Coincident(g12,g0)
    c: Coincident(g12,g4)
    c: Coincident(g12,g1)
    c: Coincident(g13,g6)
    c: Coincident(g13,g7)
    c: Coincident(g13,g10)
    c: Equal(g13,g12)
    c: Equal(g3,g2)
    c: Equal(g2,g8)
    c: Equal(g8,g9)
    c: Radius(g13) = 3.302
    c: DistanceY(g8,g8) = 12.7
FEATURE [PartDesign::Pocket] Pocket003  label="bottom shell with screw insets"
  BaseFeature = -> Pocket002
  Direction = (0,0,1)
  Length = 2.2098
  Length2 = 5
  Profile = -> Sketch010
  ReferenceAxis = -> Sketch010 [N_Axis]
  TaperAngle = -4
  Type = 0
FEATURE [PartDesign::Fillet] Fillet  label="bottom shell with interior rounded"
  Base = -> Pocket003 [Face46]
  BaseFeature = -> Pocket003
  Radius = 0.254
  SupportTransform = false
  UseAllEdges = false
FEATURE [PartDesign::Fillet] Fillet001  label="bottom shell with insets rounded"
  Base = -> Fillet [Edge132,Edge136,Edge138,Edge129,Edge123,Edge118]
  BaseFeature = -> Fillet
  Radius = 0.762
  SupportTransform = false
  UseAllEdges = false
FEATURE [PartDesign::Fillet] Fillet002  label="bottom shell with back rounded"
  Base = -> Fillet001 [Face7]
  BaseFeature = -> Fillet001
  Radius = 0.508
  SupportTransform = false
  UseAllEdges = false
FEATURE [Sketcher::SketchObject] Sketch011  label="bottom shell lip plan"
  ExternalGeometry = -> [Fillet002]
  FullyConstrained = true
  MapMode = 5
  Support = -> [Fillet002]
  sketch-geometry (32):
    g0: LineSegment StartX=-14.9225 StartY=37.0205 StartZ=0 EndX=-14.2875 EndY=37.0205 EndZ=0
    g1: LineSegment StartX=-14.2875 StartY=37.0205 StartZ=0 EndX=-12.7 EndY=37.0205 EndZ=0
    g2: LineSegment StartX=-12.7 StartY=37.0205 StartZ=0 EndX=-12.7 EndY=38.608 EndZ=0
    g3: LineSegment StartX=-12.7 StartY=38.608 StartZ=0 EndX=-12.7 EndY=39.243 EndZ=0
    g4: LineSegment StartX=-12.7 StartY=39.243 StartZ=0 EndX=12.7 EndY=39.243 EndZ=0
    g5: LineSegment StartX=12.7 StartY=39.243 StartZ=0 EndX=12.7 EndY=38.608 EndZ=0
    g6: LineSegment StartX=12.7 StartY=38.608 StartZ=0 EndX=12.7 EndY=37.0205 EndZ=0
    g7: LineSegment StartX=12.7 StartY=37.0205 StartZ=0 EndX=14.2875 EndY=37.0205 EndZ=0
    g8: LineSegment StartX=14.2875 StartY=37.0205 StartZ=0 EndX=14.9225 EndY=37.0205 EndZ=0
    g9: LineSegment StartX=14.9225 StartY=37.0205 StartZ=0 EndX=14.9225 EndY=1.0795 EndZ=0
    g10: LineSegment StartX=14.9225 StartY=1.0795 StartZ=0 EndX=14.2875 EndY=1.0795 EndZ=0
    g11: LineSegment StartX=14.2875 StartY=1.0795 StartZ=0 EndX=12.7 EndY=1.0795 EndZ=0
    g12: LineSegment StartX=12.7 StartY=1.0795 StartZ=0 EndX=12.7 EndY=-0.508 EndZ=0
    g13: LineSegment StartX=12.7 StartY=-0.508 StartZ=0 EndX=12.7 EndY=-1.143 EndZ=0
    g14: LineSegment StartX=12.7 StartY=-1.143 StartZ=0 EndX=-12.7 EndY=-1.143 EndZ=0
    g15: LineSegment StartX=-12.7 StartY=-1.143 StartZ=0 EndX=-12.7 EndY=-0.508 EndZ=0
    g16: LineSegment StartX=-12.7 StartY=-0.508 StartZ=0 EndX=-12.7 EndY=1.0795 EndZ=0
    g17: LineSegment StartX=-12.7 StartY=1.0795 StartZ=0 EndX=-14.2875 EndY=1.0795 EndZ=0
    g18: LineSegment StartX=-14.2875 StartY=1.0795 StartZ=0 EndX=-14.9225 EndY=1.0795 EndZ=0
    g19: LineSegment StartX=-14.9225 StartY=1.0795 StartZ=0 EndX=-14.9225 EndY=37.0205 EndZ=0
    g20: LineSegment StartX=-14.2875 StartY=37.0205 StartZ=0 EndX=-14.2875 EndY=1.0795 EndZ=0
    g21: LineSegment StartX=14.2875 StartY=1.0795 StartZ=0 EndX=14.2875 EndY=37.0205 EndZ=0
    g22: LineSegment StartX=12.7 StartY=38.608 StartZ=0 EndX=-12.7 EndY=38.608 EndZ=0
    g23: LineSegment StartX=-12.7 StartY=-0.508 StartZ=0 EndX=12.7 EndY=-0.508 EndZ=0
    g24: ArcOfCircle CenterX=-12.7 CenterY=37.0205 CenterZ=0 NormalX=0 NormalY=0 NormalZ=1 AngleXU=0 Radius=1.5875 StartAngle=1.5708 EndAngle=3.14159
    g25: ArcOfCircle CenterX=-12.7 CenterY=37.0205 CenterZ=0 NormalX=0 NormalY=0 NormalZ=1 AngleXU=0 Radius=2.2225 StartAngle=1.5708 EndAngle=3.14159
    g26: ArcOfCircle CenterX=-12.7 CenterY=1.0795 CenterZ=0 NormalX=0 NormalY=0 NormalZ=1 AngleXU=0 Radius=1.5875 StartAngle=3.14159 EndAngle=4.71239
    g27: ArcOfCircle CenterX=-12.7 CenterY=1.0795 CenterZ=0 NormalX=0 NormalY=0 NormalZ=1 AngleXU=0 Radius=2.2225 StartAngle=3.14159 EndAngle=4.71239
    g28: ArcOfCircle CenterX=12.7 CenterY=37.0205 CenterZ=0 NormalX=0 NormalY=0 NormalZ=1 AngleXU=0 Radius=1.5875 StartAngle=2e-16 EndAngle=1.5708
    g29: ArcOfCircle CenterX=12.7 CenterY=37.0205 CenterZ=0 NormalX=0 NormalY=0 NormalZ=1 AngleXU=0 Radius=2.2225 StartAngle=9e-16 EndAngle=1.5708
    g30: ArcOfCircle CenterX=12.7 CenterY=1.0795 CenterZ=0 NormalX=0 NormalY=0 NormalZ=1 AngleXU=0 Radius=1.5875 StartAngle=4.71239 EndAngle=6.28319
    g31: ArcOfCircle CenterX=12.7 CenterY=1.0795 CenterZ=0 NormalX=0 NormalY=0 NormalZ=1 AngleXU=0 Radius=2.2225 StartAngle=4.71239 EndAngle=6.28319
  constraints (80):
    c: Horizontal(g0)
    c: Coincident(g0,g1)
    c: Coincident(g1,g-3)
    c: Horizontal(g1)
    c: Coincident(g1,g2)
    c: Vertical(g2)
    c: Coincident(g2,g3)
    c: Vertical(g3)
    c: Coincident(g3,g4)
    c: Horizontal(g4)
    c: Coincident(g4,g5)
    c: Vertical(g5)
    c: Coincident(g5,g6)
    c: Coincident(g6,g-4)
    c: Vertical(g6)
    c: Coincident(g6,g7)
    c: Horizontal(g7)
    c: Coincident(g7,g8)
    c: Horizontal(g8)
    c: Coincident(g8,g9)
    c: Vertical(g9)
    c: Coincident(g9,g10)
    c: Horizontal(g10)
    c: Coincident(g10,g11)
    c: Coincident(g11,g-5)
    c: Coincident(g11,g12)
    c: Vertical(g12)
    c: Coincident(g12,g13)
    c: Vertical(g13)
    c: Coincident(g13,g14)
    c: Coincident(g14,g15)
    c: Vertical(g15)
    c: Coincident(g15,g16)
    c: Coincident(g16,g-6)
    c: Vertical(g16)
    c: Coincident(g16,g17)
    c: Horizontal(g17)
    c: Coincident(g17,g18)
    c: Horizontal(g18)
    c: Coincident(g18,g19)
    c: Coincident(g19,g0)
    c: Vertical(g19)
    c: Horizontal(g11)
    c: Coincident(g20,g0)
    c: Coincident(g20,g17)
    c: Vertical(g20)
    c: Coincident(g21,g10)
    c: Coincident(g21,g7)
    c: Vertical(g21)
    c: Coincident(g22,g5)
    c: Coincident(g22,g2)
    c: Horizontal(g22)
    c: Coincident(g23,g15)
    c: Coincident(g23,g12)
    c: Coincident(g24,g1)
    c: Coincident(g24,g22)
    c: Coincident(g24,g20)
    c: Coincident(g25,g24)
    c: Coincident(g25,g4)
    c: Coincident(g25,g19)
    c: Coincident(g26,g16)
    c: Coincident(g26,g20)
    c: Coincident(g26,g23)
    c: Coincident(g27,g26)
    c: Coincident(g27,g19)
    c: Coincident(g27,g14)
    c: Coincident(g28,g6)
    c: Coincident(g28,g22)
    c: Coincident(g28,g21)
    c: Coincident(g29,g28)
    c: Coincident(g29,g4)
    c: Coincident(g29,g9)
    c: Coincident(g30,g11)
    c: Coincident(g30,g21)
    c: Coincident(g30,g23)
    c: Coincident(g31,g30)
    c: Coincident(g31,g14)
    c: Equal(g24,g-3)
    c: Coincident(g9,g31)
    c: DistanceX(g18,g18) = 0.635
FEATURE [PartDesign::Pad] Pad007  label="bottom shell with lip"
  BaseFeature = -> Fillet002
  Direction = (0,0,1)
  Length = 0.508
  Length2 = 10
  Profile = -> Sketch011
  ReferenceAxis = -> Sketch011 [N_Axis]
  Type = 0
FEATURE [Sketcher::SketchObject] Sketch012  label="bottom shell jack port plan"
  FullyConstrained = true
  MapMode = 5
  Placement = pos=(0,-1.143,0) rot=(1,0,0;1.5708rad)
  Support = -> [Pad007]
  sketch-geometry (4):
    g0: ArcOfCircle CenterX=0 CenterY=0 CenterZ=0 NormalX=0 NormalY=0 NormalZ=1 AngleXU=0 Radius=2.794 StartAngle=3.14159 EndAngle=6.28319
    g1: LineSegment StartX=-2.794 StartY=3e-16 StartZ=0 EndX=-2.794 EndY=2.54 EndZ=0
    g2: LineSegment StartX=-2.794 StartY=2.54 StartZ=0 EndX=2.794 EndY=2.54 EndZ=0
    g3: LineSegment StartX=2.794 StartY=2.54 StartZ=0 EndX=2.794 EndY=-9e-16 EndZ=0
  constraints (12):
    c: Coincident(g0,g-1)
    c: PointOnObject(g0,g-1)
    c: PointOnObject(g0,g-1)
    c: Vertical(g1)
    c: Coincident(g1,g2)
    c: Horizontal(g2)
    c: Coincident(g2,g3)
    c: Coincident(g3,g0)
    c: Vertical(g3)
    c: Coincident(g1,g0)
    c: DistanceX(g2,g2) = 5.588
    c: DistanceY(g3,g3) = 2.54
FEATURE [PartDesign::Pocket] Pocket004  label="bottom shell with jack port"
  BaseFeature = -> Pad007
  Direction = (0,1,-2e-16)
  Length = 5.08
  Length2 = 5
  Midplane = true
  Profile = -> Sketch012
  ReferenceAxis = -> Sketch012 [N_Axis]
  Type = 0
FEATURE [Sketcher::SketchObject] Sketch013  label="bottom shell board guide plan"
  ExternalGeometry = -> [Pocket004]
  FullyConstrained = true
  MapMode = 5
  Placement = pos=(0,0,-4.1402) rot=(0,0,1;0rad)
  Support = -> [Pocket004]
  sketch-geometry (13):
    g0: LineSegment StartX=0 StartY=-0.254 StartZ=0 EndX=12.8905 EndY=-0.254 EndZ=0
    g1: LineSegment StartX=12.8905 StartY=-0.254 StartZ=0 EndX=12.8905 EndY=38.354 EndZ=0
    g2: LineSegment StartX=12.8905 StartY=38.354 StartZ=0 EndX=-12.8905 EndY=38.354 EndZ=0
    g3: LineSegment StartX=-12.8905 StartY=38.354 StartZ=0 EndX=-12.8905 EndY=-0.254 EndZ=0
    g4: LineSegment StartX=-12.8905 StartY=-0.254 StartZ=0 EndX=0 EndY=-0.254 EndZ=0
    g5: LineSegment StartX=-12.8905 StartY=30.6705 StartZ=0 EndX=-14.379 EndY=30.6705 EndZ=0
    g6: LineSegment StartX=-14.379 StartY=30.6705 StartZ=0 EndX=-14.379 EndY=29.0703 EndZ=0
    g7: LineSegment StartX=-14.379 StartY=29.0703 StartZ=0 EndX=-12.8905 EndY=29.0703 EndZ=0
    g8: LineSegment StartX=-12.8905 StartY=29.0703 StartZ=0 EndX=-12.8905 EndY=30.6705 EndZ=0
    g9: LineSegment StartX=12.8905 StartY=9.0297 StartZ=0 EndX=14.379 EndY=9.0297 EndZ=0
    g10: LineSegment StartX=14.379 StartY=9.0297 StartZ=0 EndX=14.379 EndY=7.4295 EndZ=0
    g11: LineSegment StartX=14.379 StartY=7.4295 StartZ=0 EndX=12.8905 EndY=7.4295 EndZ=0
    g12: LineSegment StartX=12.8905 StartY=7.4295 StartZ=0 EndX=12.8905 EndY=9.0297 EndZ=0
  constraints (39):
    c: PointOnObject(g0,g-2)
    c: Horizontal(g0)
    c: Coincident(g0,g1)
    c: Vertical(g1)
    c: Coincident(g1,g2)
    c: Horizontal(g2)
    c: Coincident(g2,g3)
    c: Vertical(g3)
    c: Coincident(g3,g4)
    c: Coincident(g4,g0)
    c: Horizontal(g4)
    c: Equal(g4,g0)
    c: DistanceX(g2,g2) = 25.781
    c: DistanceY(g1,g1) = 38.608
    c: DistanceY(g0,g-1) = 0.254
    c: Coincident(g5,g6)
    c: Coincident(g6,g7)
    c: Coincident(g7,g8)
    c: Coincident(g8,g5)
    c: Horizontal(g5)
    c: Horizontal(g7)
    c: Vertical(g6)
    c: Vertical(g8)
    c: PointOnObject(g5,g3)
    c: Coincident(g9,g10)
    c: Coincident(g10,g11)
    c: Coincident(g11,g12)
    c: Coincident(g12,g9)
    c: Horizontal(g9)
    c: Horizontal(g11)
    c: Vertical(g10)
    c: Vertical(g12)
    c: PointOnObject(g9,g1)
    c: PointOnObject(g-4,g11)
    c: PointOnObject(g-4,g9)
    c: PointOnObject(g-3,g5)
    c: PointOnObject(g-3,g7)
    c: Equal(g7,g9)
    c: DistanceX(g5,g-3) = 0.381
FEATURE [PartDesign::Pad] Pad008  label="bottom shell with board guides"
  BaseFeature = -> Pocket004
  Direction = (0,0,1)
  Length = 1.27
  Length2 = 10
  Profile = -> Sketch013
  ReferenceAxis = -> Sketch013 [N_Axis]
  TaperAngle = -4
  Type = 0
FEATURE [PartDesign::Body] Body007  label="bottom shell body"
  Group = -> [Sketch006,Pad006,Sketch007,Pocket,Sketch008,Pocket001,Sketch009,Pocket002,Sketch010,Pocket003,Fillet,Fillet001,Fillet002,Sketch011,Pad007,Sketch012,Pocket004,Sketch013,Pad008]
  Origin = -> Origin007
  Tip = -> Pad008
FEATURE [PartDesign::FeatureBase] Clone004
  BaseFeature = -> Body007
FEATURE [PartDesign::Body] Body008  label="bottom shell clone"
  Group = -> [Clone004]
  Origin = -> Origin008
  Tip = -> Clone004
FEATURE [Sketcher::SketchObject] Sketch014  label="top shell outline"
  FullyConstrained = true
  MapMode = 5
  Support = -> [XY_Plane009]
  sketch-geometry (37):
    g0: LineSegment StartX=0 StartY=1.0795 StartZ=0 EndX=12.7 EndY=1.0795 EndZ=0
    g1: LineSegment StartX=12.7 StartY=1.0795 StartZ=0 EndX=14.2875 EndY=1.0795 EndZ=0
    g2: LineSegment StartX=14.2875 StartY=1.0795 StartZ=0 EndX=15.875 EndY=1.0795 EndZ=0
    g3: LineSegment StartX=12.7 StartY=1.0795 StartZ=0 EndX=12.7 EndY=37.0205 EndZ=0
    g4: LineSegment StartX=12.7 StartY=37.0205 StartZ=0 EndX=14.2875 EndY=37.0205 EndZ=0
    g5: LineSegment StartX=14.2875 StartY=37.0205 StartZ=0 EndX=15.875 EndY=37.0205 EndZ=0
    g6: LineSegment StartX=12.7 StartY=40.1955 StartZ=0 EndX=12.7 EndY=38.608 EndZ=0
    g7: LineSegment StartX=12.7 StartY=38.608 StartZ=0 EndX=12.7 EndY=37.0205 EndZ=0
    g8: LineSegment StartX=12.7 StartY=37.0205 StartZ=0 EndX=-12.7 EndY=37.0205 EndZ=0
    g9: LineSegment StartX=-12.7 StartY=37.0205 StartZ=0 EndX=-12.7 EndY=38.608 EndZ=0
    g10: LineSegment StartX=-12.7 StartY=38.608 StartZ=0 EndX=-12.7 EndY=40.1955 EndZ=0
    g11: LineSegment StartX=-15.875 StartY=37.0205 StartZ=0 EndX=-14.2875 EndY=37.0205 EndZ=0
    g12: LineSegment StartX=-14.2875 StartY=37.0205 StartZ=0 EndX=-12.7 EndY=37.0205 EndZ=0
    g13: LineSegment StartX=-12.7 StartY=37.0205 StartZ=0 EndX=-12.7 EndY=1.0795 EndZ=0
    g14: LineSegment StartX=-12.7 StartY=1.0795 StartZ=0 EndX=-14.2875 EndY=1.0795 EndZ=0
    g15: LineSegment StartX=-14.2875 StartY=1.0795 StartZ=0 EndX=-15.875 EndY=1.0795 EndZ=0
    g16: LineSegment StartX=-12.7 StartY=-2.0955 StartZ=0 EndX=-12.7 EndY=-0.508 EndZ=0
    g17: LineSegment StartX=-12.7 StartY=-0.508 StartZ=0 EndX=-12.7 EndY=1.0795 EndZ=0
    g18: LineSegment StartX=-12.7 StartY=1.0795 StartZ=0 EndX=0 EndY=1.0795 EndZ=0
    g19: LineSegment StartX=12.7 StartY=1.0795 StartZ=0 EndX=12.7 EndY=-0.508 EndZ=0
    g20: LineSegment StartX=12.7 StartY=-0.508 StartZ=0 EndX=12.7 EndY=-2.0955 EndZ=0
    g21: LineSegment StartX=-14.2875 StartY=37.0205 StartZ=0 EndX=-14.2875 EndY=1.0795 EndZ=0
    g22: LineSegment StartX=-15.875 StartY=1.0795 StartZ=0 EndX=-15.875 EndY=37.0205 EndZ=0
    g23: LineSegment StartX=14.2875 StartY=1.0795 StartZ=0 EndX=14.2875 EndY=37.0205 EndZ=0
    g24: LineSegment StartX=15.875 StartY=1.0795 StartZ=0 EndX=15.875 EndY=37.0205 EndZ=0
    g25: LineSegment StartX=12.7 StartY=38.608 StartZ=0 EndX=-12.7 EndY=38.608 EndZ=0
    g26: LineSegment StartX=-12.7 StartY=40.1955 StartZ=0 EndX=12.7 EndY=40.1955 EndZ=0
    g27: LineSegment StartX=-12.7 StartY=-0.508 StartZ=0 EndX=12.7 EndY=-0.508 EndZ=0
    g28: LineSegment StartX=12.7 StartY=-2.0955 StartZ=0 EndX=-12.7 EndY=-2.0955 EndZ=0
    g29: ArcOfCircle CenterX=12.7 CenterY=1.0795 CenterZ=0 NormalX=0 NormalY=0 NormalZ=1 AngleXU=0 Radius=1.5875 StartAngle=4.71239 EndAngle=6.28319
    g30: ArcOfCircle CenterX=12.7 CenterY=1.0795 CenterZ=0 NormalX=0 NormalY=0 NormalZ=1 AngleXU=0 Radius=3.175 StartAngle=4.71239 EndAngle=6.28319
    g31: ArcOfCircle CenterX=12.7 CenterY=37.0205 CenterZ=0 NormalX=0 NormalY=0 NormalZ=1 AngleXU=0 Radius=1.5875 StartAngle=0 EndAngle=1.5708
    g32: ArcOfCircle CenterX=12.7 CenterY=37.0205 CenterZ=0 NormalX=0 NormalY=0 NormalZ=1 AngleXU=0 Radius=3.175 StartAngle=0 EndAngle=1.5708
    g33: ArcOfCircle CenterX=-12.7 CenterY=37.0205 CenterZ=0 NormalX=0 NormalY=0 NormalZ=1 AngleXU=0 Radius=1.5875 StartAngle=1.5708 EndAngle=3.14159
    g34: ArcOfCircle CenterX=-12.7 CenterY=37.0205 CenterZ=0 NormalX=0 NormalY=0 NormalZ=1 AngleXU=0 Radius=3.175 StartAngle=1.5708 EndAngle=3.14159
    g35: ArcOfCircle CenterX=-12.7 CenterY=1.0795 CenterZ=0 NormalX=0 NormalY=0 NormalZ=1 AngleXU=0 Radius=1.5875 StartAngle=3.14159 EndAngle=4.71239
    g36: ArcOfCircle CenterX=-12.7 CenterY=1.0795 CenterZ=0 NormalX=0 NormalY=0 NormalZ=1 AngleXU=0 Radius=3.175 StartAngle=3.14159 EndAngle=4.71239
  constraints (95):
    c: Coincident(g0,g1)
    c: Horizontal(g1)
    c: Coincident(g1,g2)
    c: Horizontal(g2)
    c: Coincident(g0,g3)
    c: Vertical(g3)
    c: Coincident(g3,g4)
    c: Horizontal(g4)
    c: Coincident(g4,g5)
    c: Horizontal(g5)
    c: Vertical(g6)
    c: Coincident(g6,g7)
    c: Coincident(g7,g3)
    c: Vertical(g7)
    c: Coincident(g7,g8)
    c: Horizontal(g8)
    c: Coincident(g8,g9)
    c: Vertical(g9)
    c: Coincident(g9,g10)
    c: Vertical(g10)
    c: Horizontal(g11)
    c: Coincident(g11,g12)
    c: Coincident(g12,g8)
    c: Horizontal(g12)
    c: Coincident(g12,g13)
    c: Vertical(g13)
    c: Coincident(g13,g14)
    c: Horizontal(g14)
    c: Coincident(g14,g15)
    c: Horizontal(g15)
    c: Vertical(g16)
    c: Coincident(g16,g17)
    c: Coincident(g17,g13)
    c: Vertical(g17)
    c: Coincident(g17,g18)
    c: Coincident(g18,g0)
    c: Coincident(g0,g19)
    c: Vertical(g19)
    c: Coincident(g19,g20)
    c: Vertical(g20)
    c: Horizontal(g18)
    c: Horizontal(g0)
    c: Coincident(g21,g11)
    c: Vertical(g21)
    c: Coincident(g22,g15)
    c: Coincident(g22,g11)
    c: Vertical(g22)
    c: Coincident(g23,g1)
    c: Coincident(g23,g4)
    c: Vertical(g23)
    c: Coincident(g24,g2)
    c: Coincident(g24,g5)
    c: Vertical(g24)
    c: Coincident(g25,g6)
    c: Coincident(g25,g9)
    c: Horizontal(g25)
    c: Coincident(g26,g10)
    c: Coincident(g26,g6)
    c: Coincident(g27,g16)
    c: Coincident(g27,g19)
    c: Coincident(g28,g20)
    c: Coincident(g28,g16)
    c: Coincident(g14,g21)
    c: Horizontal(g26)
    c: Coincident(g29,g0)
    c: Coincident(g29,g27)
    c: Coincident(g29,g23)
    c: Coincident(g30,g29)
    c: Coincident(g30,g28)
    c: Coincident(g30,g24)
    c: Coincident(g31,g3)
    c: Coincident(g31,g23)
    c: Coincident(g31,g25)
    c: Coincident(g32,g31)
    c: Coincident(g32,g24)
    c: Coincident(g32,g26)
    c: Coincident(g33,g8)
    c: Coincident(g33,g25)
    c: Coincident(g33,g21)
    c: Coincident(g34,g33)
    c: Coincident(g34,g26)
    c: Coincident(g34,g22)
    c: Coincident(g35,g13)
    c: Coincident(g35,g21)
    c: Coincident(g35,g27)
    c: Coincident(g36,g35)
    c: Coincident(g36,g22)
    c: Coincident(g36,g28)
    c: Equal(g18,g0)
    c: DistanceX(g35,g29) = 25.4
    c: DistanceX(g22,g35) = 3.175
    c: DistanceX(g15,g15) = 1.5875
    c: DistanceY(g27,g25) = 39.116
    c: PointOnObject(g0,g-2)
    c: DistanceY(g19,g-1) = 0.508
FEATURE [PartDesign::Pad] Pad009  label="top shell block"
  Direction = (0,0,1)
  Length = 4.7625
  Length2 = 10
  Profile = -> Sketch014
  ReferenceAxis = -> Sketch014 [N_Axis]
  TaperAngle = -4
  Type = 0
FEATURE [Sketcher::SketchObject] Sketch015  label="top shell hollow plan"
  ExternalGeometry = -> [Pad009]
  FullyConstrained = true
  MapMode = 5
  Placement = pos=(0,0,0) rot=(1,0,0;3.14159rad)
  Support = -> [Pad009]
  sketch-geometry (27):
    g0: LineSegment StartX=0 StartY=0 StartZ=0 EndX=-12.7 EndY=0 EndZ=0
    g1: LineSegment StartX=-12.7 StartY=0 StartZ=0 EndX=-12.7 EndY=-38.1 EndZ=0
    g2: LineSegment StartX=-12.7 StartY=-38.1 StartZ=0 EndX=12.7 EndY=-38.1 EndZ=0
    g3: LineSegment StartX=12.7 StartY=-38.1 StartZ=0 EndX=12.7 EndY=0 EndZ=0
    g4: LineSegment StartX=12.7 StartY=0 StartZ=0 EndX=0 EndY=0 EndZ=0
    g5: LineSegment StartX=-12.7 StartY=0 StartZ=0 EndX=-8.89 EndY=0 EndZ=0
    g6: LineSegment StartX=-8.89 StartY=0 StartZ=0 EndX=-8.89 EndY=-3.81 EndZ=0
    g7: LineSegment StartX=12.7 StartY=-38.1 StartZ=0 EndX=8.89 EndY=-38.1 EndZ=0
    g8: LineSegment StartX=8.89 StartY=-38.1 StartZ=0 EndX=8.89 EndY=-34.29 EndZ=0
    g9: Circle CenterX=-8.89 CenterY=-3.81 CenterZ=0 NormalX=0 NormalY=0 NormalZ=1 AngleXU=0 Radius=2.794
    g10: Circle CenterX=8.89 CenterY=-34.29 CenterZ=0 NormalX=0 NormalY=0 NormalZ=1 AngleXU=0 Radius=2.794
    g11: LineSegment StartX=-14.2875 StartY=-1.0795 StartZ=0 EndX=-12.7 EndY=-1.0795 EndZ=0
    g12: LineSegment StartX=-12.7 StartY=-1.0795 StartZ=0 EndX=-12.7 EndY=0.508 EndZ=0
    g13: LineSegment StartX=-12.7 StartY=0.508 StartZ=0 EndX=12.7 EndY=0.508 EndZ=0
    g14: LineSegment StartX=12.7 StartY=0.508 StartZ=0 EndX=12.7 EndY=-1.0795 EndZ=0
    g15: LineSegment StartX=12.7 StartY=-1.0795 StartZ=0 EndX=14.2875 EndY=-1.0795 EndZ=0
    g16: LineSegment StartX=14.2875 StartY=-1.0795 StartZ=0 EndX=14.2875 EndY=-37.0205 EndZ=0
    g17: LineSegment StartX=14.2875 StartY=-37.0205 StartZ=0 EndX=12.7 EndY=-37.0205 EndZ=0
    g18: LineSegment StartX=12.7 StartY=-37.0205 StartZ=0 EndX=12.7 EndY=-38.608 EndZ=0
    g19: LineSegment StartX=12.7 StartY=-38.608 StartZ=0 EndX=-12.7 EndY=-38.608 EndZ=0
    g20: LineSegment StartX=-12.7 StartY=-38.608 StartZ=0 EndX=-12.7 EndY=-37.0205 EndZ=0
    g21: LineSegment StartX=-12.7 StartY=-37.0205 StartZ=0 EndX=-14.2875 EndY=-37.0205 EndZ=0
    g22: LineSegment StartX=-14.2875 StartY=-37.0205 StartZ=0 EndX=-14.2875 EndY=-1.0795 EndZ=0
    g23: ArcOfCircle CenterX=-12.7 CenterY=-1.0795 CenterZ=0 NormalX=0 NormalY=0 NormalZ=1 AngleXU=0 Radius=1.5875 StartAngle=1.5708 EndAngle=3.14159
    g24: ArcOfCircle CenterX=12.7 CenterY=-1.0795 CenterZ=0 NormalX=0 NormalY=0 NormalZ=1 AngleXU=0 Radius=1.5875 StartAngle=0 EndAngle=1.5708
    g25: ArcOfCircle CenterX=-12.7 CenterY=-37.0205 CenterZ=0 NormalX=0 NormalY=0 NormalZ=1 AngleXU=0 Radius=1.5875 StartAngle=3.14159 EndAngle=4.71239
    g26: ArcOfCircle CenterX=12.7 CenterY=-37.0205 CenterZ=0 NormalX=0 NormalY=0 NormalZ=1 AngleXU=0 Radius=1.5875 StartAngle=4.71239 EndAngle=6.28319
  constraints (70):
    c: Horizontal(g0)
    c: Coincident(g0,g1)
    c: Vertical(g1)
    c: Coincident(g1,g2)
    c: Horizontal(g2)
    c: Coincident(g2,g3)
    c: Vertical(g3)
    c: Coincident(g3,g4)
    c: Coincident(g4,g0)
    c: Horizontal(g4)
    c: Equal(g4,g0)
    c: Coincident(g0,g-1)
    c: DistanceX(g2,g2) = 25.4
    c: DistanceY(g3,g3) = 38.1
    c: Coincident(g0,g5)
    c: Coincident(g5,g6)
    c: Vertical(g6)
    c: Coincident(g2,g7)
    c: Coincident(g7,g8)
    c: Vertical(g8)
    c: Equal(g7,g8)
    c: Equal(g8,g6)
    c: Equal(g6,g5)
    c: Horizontal(g5)
    c: Horizontal(g7)
    c: DistanceY(g2,g8) = 3.81
    c: Coincident(g9,g6)
    c: Coincident(g10,g8)
    c: Equal(g9,g10)
    c: Diameter(g9) = 5.588
    c: Coincident(g11,g-3)
    c: Horizontal(g11)
    c: Coincident(g11,g12)
    c: Vertical(g12)
    c: Coincident(g12,g13)
    c: Horizontal(g13)
    c: Coincident(g13,g14)
    c: Coincident(g14,g-4)
    c: Vertical(g14)
    c: Coincident(g14,g15)
    c: Horizontal(g15)
    c: Coincident(g15,g16)
    c: Vertical(g16)
    c: Coincident(g16,g17)
    c: Coincident(g17,g-5)
    c: Horizontal(g17)
    c: Coincident(g17,g18)
    c: Vertical(g18)
    c: Coincident(g18,g19)
    c: Coincident(g19,g20)
    c: Coincident(g20,g-6)
    c: Coincident(g20,g21)
    c: Horizontal(g21)
    c: Coincident(g21,g22)
    c: Coincident(g22,g11)
    c: Vertical(g22)
    c: Vertical(g20)
    c: Coincident(g23,g11)
    c: Coincident(g23,g13)
    c: Coincident(g23,g22)
    c: Coincident(g24,g14)
    c: Coincident(g24,g13)
    c: Coincident(g24,g16)
    c: Coincident(g25,g20)
    c: Coincident(g25,g22)
    c: Coincident(g26,g17)
    c: Coincident(g26,g16)
    c: Coincident(g26,g19)
    c: Coincident(g25,g19)
    c: DistanceX(g-3,g22) = 1.5875
FEATURE [PartDesign::Pocket] Pocket005  label="top shell with hollow"
  BaseFeature = -> Pad009
  Direction = (0,0,1)
  Length = 3.175
  Length2 = 5
  Profile = -> Sketch015
  ReferenceAxis = -> Sketch015 [N_Axis]
  TaperAngle = -4
  Type = 0
FEATURE [PartDesign::Fillet] Fillet003  label="top shell with rounded back"
  Base = -> Pocket005 [Face4]
  BaseFeature = -> Pocket005
  Radius = 0.508
  SupportTransform = false
  UseAllEdges = false
FEATURE [Sketcher::SketchObject] Sketch016  label="top shell post extension plan"
  ExternalGeometry = -> [Fillet003]
  FullyConstrained = true
  MapMode = 5
  Placement = pos=(0,0,0) rot=(1,0,0;3.14159rad)
  Support = -> [Fillet003]
  sketch-geometry (2):
    g0: Circle CenterX=-8.89 CenterY=-3.81 CenterZ=0 NormalX=0 NormalY=0 NormalZ=1 AngleXU=0 Radius=2.794
    g1: Circle CenterX=8.89 CenterY=-34.29 CenterZ=0 NormalX=0 NormalY=0 NormalZ=1 AngleXU=0 Radius=2.794
  constraints (4):
    c: Coincident(g0,g-3)
    c: Coincident(g1,g-4)
    c: Equal(g0,g1)
    c: Equal(g1,g-3)
FEATURE [PartDesign::Pad] Pad010  label="top shell with post extensions"
  BaseFeature = -> Fillet003
  Direction = (0,0,-1)
  Length = 2.54
  Length2 = 10
  Profile = -> Sketch016
  ReferenceAxis = -> Sketch016 [N_Axis]
  TaperAngle = 4
  Type = 0
FEATURE [Sketcher::SketchObject] Sketch017  label="top shell screw hole plan"
  ExternalGeometry = -> [Pad010]
  FullyConstrained = true
  MapMode = 5
  Placement = pos=(0,0,-2.54) rot=(1,0,0;3.14159rad)
  Support = -> [Pad010]
  sketch-geometry (2):
    g0: Circle CenterX=-8.89 CenterY=-3.81 CenterZ=0 NormalX=0 NormalY=0 NormalZ=1 AngleXU=0 Radius=1.143
    g1: Circle CenterX=8.89 CenterY=-34.29 CenterZ=0 NormalX=0 NormalY=0 NormalZ=1 AngleXU=0 Radius=1.143
  constraints (4):
    c: Coincident(g0,g-3)
    c: Coincident(g1,g-4)
    c: Equal(g0,g1)
    c: Diameter(g0) = 2.286
FEATURE [PartDesign::Pocket] Pocket006  label="top shell with screw holes"
  BaseFeature = -> Pad010
  Direction = (0,0,1)
  Length = 5
  Length2 = 5
  Profile = -> Sketch017
  ReferenceAxis = -> Sketch017 [N_Axis]
  Type = 1
FEATURE [PartDesign::Fillet] Fillet004  label="top shell with interior rounded"
  Base = -> Pocket006 [Face29]
  BaseFeature = -> Pocket006
  Radius = 0.254
  SupportTransform = false
  UseAllEdges = false
FEATURE [Sketcher::SketchObject] Sketch018  label="top shell lip plan"
  ExternalGeometry = -> [Fillet004]
  FullyConstrained = true
  MapMode = 5
  Placement = pos=(0,0,0) rot=(1,0,0;3.14159rad)
  Support = -> [Fillet004]
  sketch-geometry (21):
    g0: LineSegment StartX=0 StartY=-0.5715 StartZ=0 EndX=-13.208 EndY=-0.5715 EndZ=0
    g1: LineSegment StartX=-13.208 StartY=-0.5715 StartZ=0 EndX=-13.208 EndY=-37.5285 EndZ=0
    g2: LineSegment StartX=-13.208 StartY=-37.5285 StartZ=0 EndX=13.208 EndY=-37.5285 EndZ=0
    g3: LineSegment StartX=13.208 StartY=-37.5285 StartZ=0 EndX=13.208 EndY=-0.5715 EndZ=0
    g4: LineSegment StartX=13.208 StartY=-0.5715 StartZ=0 EndX=0 EndY=-0.5715 EndZ=0
    g5: LineSegment StartX=-15.1765 StartY=-1.0795 StartZ=0 EndX=-12.7 EndY=-1.0795 EndZ=0
    g6: LineSegment StartX=-12.7 StartY=-1.0795 StartZ=0 EndX=-12.7 EndY=1.397 EndZ=0
    g7: LineSegment StartX=-12.7 StartY=1.397 StartZ=0 EndX=12.7 EndY=1.397 EndZ=0
    g8: LineSegment StartX=12.7 StartY=1.397 StartZ=0 EndX=12.7 EndY=-1.0795 EndZ=0
    g9: LineSegment StartX=12.7 StartY=-1.0795 StartZ=0 EndX=15.1765 EndY=-1.0795 EndZ=0
    g10: LineSegment StartX=15.1765 StartY=-1.0795 StartZ=0 EndX=15.1765 EndY=-37.0205 EndZ=0
    g11: LineSegment StartX=15.1765 StartY=-37.0205 StartZ=0 EndX=12.7 EndY=-37.0205 EndZ=0
    g12: LineSegment StartX=12.7 StartY=-37.0205 StartZ=0 EndX=12.7 EndY=-39.497 EndZ=0
    g13: LineSegment StartX=12.7 StartY=-39.497 StartZ=0 EndX=-12.7 EndY=-39.497 EndZ=0
    g14: LineSegment StartX=-12.7 StartY=-39.497 StartZ=0 EndX=-12.7 EndY=-37.0205 EndZ=0
    g15: LineSegment StartX=-12.7 StartY=-37.0205 StartZ=0 EndX=-15.1765 EndY=-37.0205 EndZ=0
    g16: LineSegment StartX=-15.1765 StartY=-37.0205 StartZ=0 EndX=-15.1765 EndY=-1.0795 EndZ=0
    g17: ArcOfCircle CenterX=-12.7 CenterY=-1.0795 CenterZ=0 NormalX=0 NormalY=0 NormalZ=1 AngleXU=0 Radius=2.4765 StartAngle=1.5708 EndAngle=3.14159
    g18: ArcOfCircle CenterX=-12.7 CenterY=-37.0205 CenterZ=0 NormalX=0 NormalY=0 NormalZ=1 AngleXU=0 Radius=2.4765 StartAngle=3.14159 EndAngle=4.71239
    g19: ArcOfCircle CenterX=12.7 CenterY=-1.0795 CenterZ=0 NormalX=0 NormalY=0 NormalZ=1 AngleXU=0 Radius=2.4765 StartAngle=0 EndAngle=1.5708
    g20: ArcOfCircle CenterX=12.7 CenterY=-37.0205 CenterZ=0 NormalX=0 NormalY=0 NormalZ=1 AngleXU=0 Radius=2.4765 StartAngle=4.71239 EndAngle=6.28319
  constraints (55):
    c: PointOnObject(g0,g-2)
    c: Horizontal(g0)
    c: Coincident(g0,g1)
    c: Vertical(g1)
    c: Coincident(g1,g2)
    c: Horizontal(g2)
    c: Coincident(g2,g3)
    c: Vertical(g3)
    c: Coincident(g3,g4)
    c: Coincident(g4,g0)
    c: Horizontal(g4)
    c: Equal(g0,g4)
    c: DistanceX(g-4,g3) = 0.508
    c: DistanceY(g-4,g3) = 0.508
    c: DistanceY(g2,g-5) = 0.508
    c: Coincident(g5,g-3)
    c: Horizontal(g5)
    c: Coincident(g5,g6)
    c: Vertical(g6)
    c: Coincident(g6,g7)
    c: Horizontal(g7)
    c: Coincident(g7,g8)
    c: Coincident(g8,g-4)
    c: Vertical(g8)
    c: Coincident(g8,g9)
    c: Horizontal(g9)
    c: Coincident(g9,g10)
    c: Vertical(g10)
    c: Coincident(g10,g11)
    c: Coincident(g11,g-5)
    c: Horizontal(g11)
    c: Coincident(g11,g12)
    c: Vertical(g12)
    c: Coincident(g12,g13)
    c: Coincident(g13,g14)
    c: Coincident(g14,g-6)
    c: Vertical(g14)
    c: Coincident(g14,g15)
    c: Horizontal(g15)
    c: Coincident(g15,g16)
    c: Coincident(g16,g5)
    c: Vertical(g16)
    c: Coincident(g17,g5)
    c: Coincident(g17,g7)
    c: Coincident(g17,g16)
    c: Coincident(g18,g14)
    c: Coincident(g18,g16)
    c: Coincident(g18,g13)
    c: Coincident(g19,g8)
    c: Coincident(g19,g7)
    c: Coincident(g19,g10)
    c: Coincident(g20,g11)
    c: Coincident(g20,g10)
    c: Coincident(g20,g13)
    c: DistanceX(g16,g-3) = 0.889
FEATURE [PartDesign::Pocket] Pocket007  label="top shell with lip"
  BaseFeature = -> Fillet004
  Direction = (0,0,1)
  Length = 0.762
  Length2 = 5
  Profile = -> Sketch018
  ReferenceAxis = -> Sketch018 [N_Axis]
  Type = 0
FEATURE [Sketcher::SketchObject] Sketch019  label="top shell audio hole plan"
  FullyConstrained = true
  MapMode = 5
  Placement = pos=(0,-1.397,0) rot=(0,0.707107,0.707107;3.14159rad)
  Support = -> [Pocket007]
  sketch-geometry (4):
    g0: LineSegment StartX=-2.794 StartY=0 StartZ=0 EndX=-2.794 EndY=-2.54 EndZ=0
    g1: LineSegment StartX=-2.794 StartY=-2.54 StartZ=0 EndX=2.794 EndY=-2.54 EndZ=0
    g2: LineSegment StartX=2.794 StartY=-2.54 StartZ=0 EndX=2.794 EndY=0 EndZ=0
    g3: ArcOfCircle CenterX=0 CenterY=0 CenterZ=0 NormalX=0 NormalY=0 NormalZ=1 AngleXU=0 Radius=2.794 StartAngle=0 EndAngle=3.14159
  constraints (12):
    c: Vertical(g0)
    c: Coincident(g0,g1)
    c: Horizontal(g1)
    c: Coincident(g1,g2)
    c: PointOnObject(g2,g-1)
    c: Vertical(g2)
    c: PointOnObject(g0,g-1)
    c: Coincident(g3,g-1)
    c: Coincident(g3,g2)
    c: Coincident(g3,g0)
    c: DistanceX(g1,g1) = 5.588
    c: DistanceY(g2,g2) = 2.54
FEATURE [PartDesign::Pocket] Pocket008  label="top shell with audio hole"
  BaseFeature = -> Pocket007
  Direction = (0,-1,2e-16)
  Length = 5.08
  Length2 = 5
  Midplane = true
  Profile = -> Sketch019
  ReferenceAxis = -> Sketch019 [N_Axis]
  Type = 0
FEATURE [Sketcher::SketchObject] Sketch020  label="top shell button hole plan"
  FullyConstrained = true
  MapMode = 5
  Placement = pos=(0,0,4.7625) rot=(0,0,1;0rad)
  Support = -> [Pocket008]
  sketch-geometry (1):
    g0: Circle CenterX=0 CenterY=25.4 CenterZ=0 NormalX=0 NormalY=0 NormalZ=1 AngleXU=0 Radius=5.715
  constraints (3):
    c: PointOnObject(g0,g-2)
    c: DistanceY(g-1,g0) = 25.4
    c: Diameter(g0) = 11.43
FEATURE [PartDesign::Pocket] Pocket009  label="top shell with button hole"
  BaseFeature = -> Pocket008
  Direction = (0,0,-1)
  Length = 5
  Length2 = 5
  Profile = -> Sketch020
  ReferenceAxis = -> Sketch020 [N_Axis]
  Type = 1
FEATURE [PartDesign::Body] Body009  label="top shell body"
  Group = -> [Sketch014,Pad009,Sketch015,Pocket005,Fillet003,Sketch016,Pad010,Sketch017,Pocket006,Fillet004,Sketch018,Pocket007,Sketch019,Pocket008,Sketch020,Pocket009]
  Origin = -> Origin009
  Tip = -> Pocket009
FEATURE [App::DocumentObjectGroup] Group001  label="shell parts"
  Group = -> [Body007,Body009]
FEATURE [PartDesign::FeatureBase] Clone005
  BaseFeature = -> Body009
FEATURE [PartDesign::Body] Body010  label="top shell clone"
  Group = -> [Clone005]
  Origin = -> Origin010
  Tip = -> Clone005
FEATURE [Part::Feature] screw_4_40_3f8
  shape: bbox 5.588 x 5.588 x 11.63 mm, 5 faces (baked)
FEATURE [App::DocumentObjectGroup] Group004  label="imported"
  Group = -> [screw_4_40_3f8]
FEATURE [PartDesign::FeatureBase] Clone006
  BaseFeature = -> screw_4_40_3f8
FEATURE [PartDesign::Body] Body011  label="mockup screw 1"
  Group = -> [Clone006]
  Origin = -> Origin011
  Placement = pos=(-8.89,3.81,-5.842) rot=(1,0,0;3.14159rad)
  Tip = -> Clone006
FEATURE [PartDesign::FeatureBase] Clone007
  BaseFeature = -> screw_4_40_3f8
FEATURE [PartDesign::Body] Body012  label="mockup screw 2"
  Group = -> [Clone007]
  Origin = -> Origin012
  Placement = pos=(8.89,34.29,-5.842) rot=(1,0,0;3.14159rad)
  Tip = -> Clone007
FEATURE [App::DocumentObjectGroup] Group002  label="mockup"
  Group = -> [Body006,Body008,Body010,Body011,Body012]
FEATURE [Mesh::Feature] Mesh  label="bottom shell mesh"
FEATURE [Mesh::Feature] Mesh001  label="top shell mesh"
FEATURE [App::DocumentObjectGroup] Group003  label="meshes"
  Group = -> [Mesh,Mesh001]
